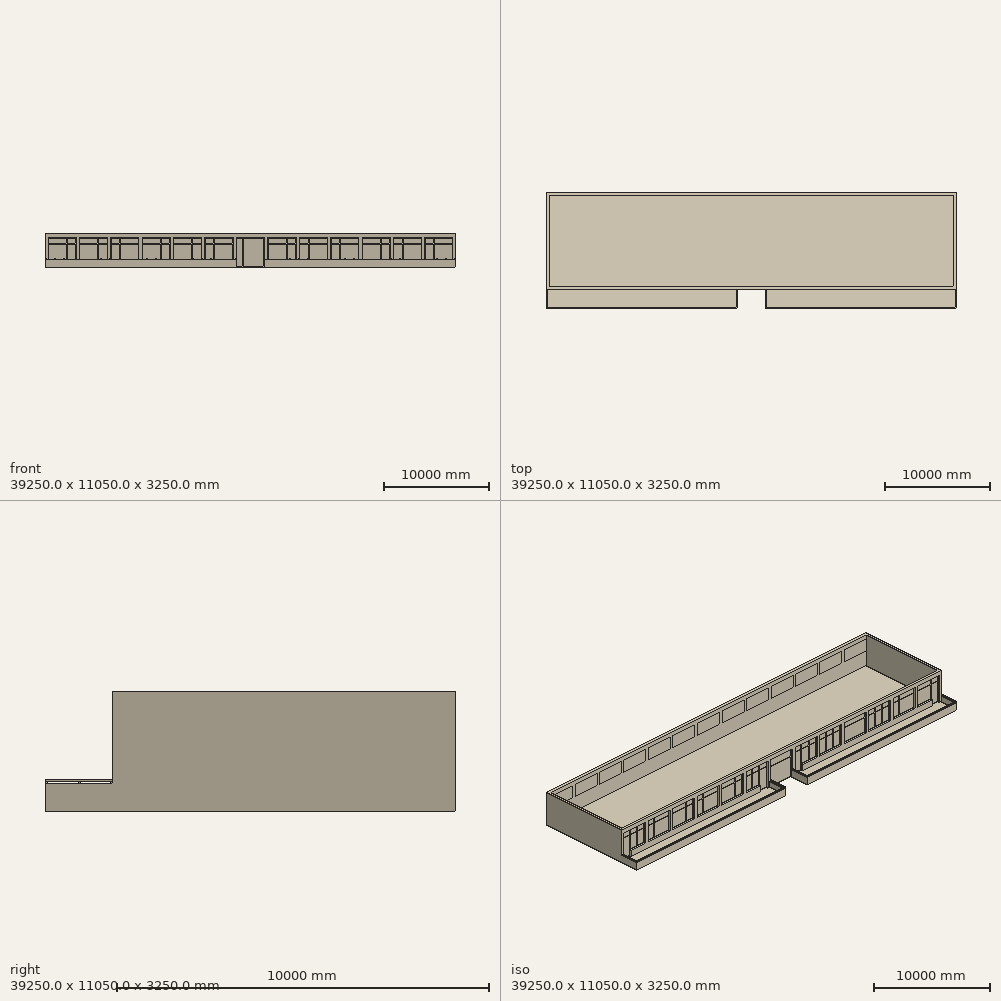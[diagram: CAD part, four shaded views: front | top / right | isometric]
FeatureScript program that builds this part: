
annotation { "Feature Type Name" : "Feature", "Feature Type Description" : "" }
export const myFeature = defineFeature(function(context is Context, id is Id, definition is map)
    precondition{}
    {
        {
            var Q0;
            Q0=qCreatedBy(makeId("Top.planeOp"),FACE);
            var sketch = newSketch(context, id + "F0", { "sketchPlane" : qUnion([Q0])});
            skLineSegment(sketch, "E0.bottom", {"start": v(0, 0) * mm, "end": v(39250, 0) * mm});
            skLineSegment(sketch, "E0.top", {"start": v(0, -9250) * mm, "end": v(39250, -9250) * mm});
            skLineSegment(sketch, "E0.left", {"start": v(0, 0) * mm, "end": v(0, -9250) * mm});
            skLineSegment(sketch, "E0.right", {"start": v(39250, 0) * mm, "end": v(39250, -9250) * mm});
            skSolve(sketch);
        }
        {
            var Q0;
            Q0=qSketchRegion(id+"F0",true);
            extrude(context, id + "F1", {"entities" : qUnion([Q0]), "depth" : 150 * mm, "offsetDistance" : 25 * mm});
        }
        {
            var Q0;
            Q0=makeQuery(id+"F1.opExtrude","CAP_FACE",FACE,{"disambiguationData":[OSD([sQuery(id+"F0.wireOp",EDGE,"E0.bottom"),sQuery(id+"F0.wireOp",EDGE,"E0.top"),sQuery(id+"F0.wireOp",EDGE,"E0.left"),sQuery(id+"F0.wireOp",EDGE,"E0.right")])],"isStart":false});
            var sketch = newSketch(context, id + "F2", { "sketchPlane" : qUnion([Q0])});
            skLineSegment(sketch, "E1.0.0", {"start": v(0, 0) * mm, "end": v(0, -9250) * mm});
            skLineSegment(sketch, "E1.0.1", {"start": v(0, -9250) * mm, "end": v(39250, -9250) * mm});
            skLineSegment(sketch, "E1.0.2", {"start": v(39250, -9250) * mm, "end": v(39250, 0) * mm});
            skLineSegment(sketch, "E1.0.3", {"start": v(39250, 0) * mm, "end": v(0, 0) * mm});
            skLineSegment(sketch, "E2.0", {"start": v(250, -250) * mm, "end": v(250, -9000) * mm});
            skLineSegment(sketch, "E2.1", {"start": v(39000, -250) * mm, "end": v(250, -250) * mm});
            skLineSegment(sketch, "E2.2", {"start": v(39000, -9000) * mm, "end": v(39000, -250) * mm});
            skLineSegment(sketch, "E2.3", {"start": v(250, -9000) * mm, "end": v(39000, -9000) * mm});
            skSolve(sketch);
        }
        {
            var Q0;
            Q0=qSketchRegion(id+"F2",true);
            extrude(context, id + "F3", {"entities" : qUnion([Q0]), "operationType" : NewBodyOperationType.ADD, "depth" : 3100 * mm, "offsetDistance" : 25 * mm});
        }
        {
            var Q0;
            Q0=makeQuery(id+"F3.boolean.opBoolean","MERGE",FACE,{"derivedFrom":[makeQuery(id+"F1.opExtrude","SWEPT_FACE",FACE,{"disambiguationData":[OSD([sQuery(id+"F0.wireOp",EDGE,"E0.top")])]}),makeQuery(id+"F3.opExtrude","SWEPT_FACE",FACE,{"disambiguationData":[OSD([sQuery(id+"F2.wireOp",EDGE,"E1.0.1")])]})]});
            var sketch = newSketch(context, id + "F4", { "sketchPlane" : qUnion([Q0])});
            skLineSegment(sketch, "E3", {"start": v(1150, 150) * mm, "end": v(250, 150) * mm});
            skLineSegment(sketch, "E4", {"start": v(250, 150) * mm, "end": v(250, 2850) * mm});
            skLineSegment(sketch, "E5", {"start": v(250, 2850) * mm, "end": v(2950, 2850) * mm});
            skLineSegment(sketch, "E6", {"start": v(2950, 2850) * mm, "end": v(2950, 750) * mm});
            skLineSegment(sketch, "E7", {"start": v(2950, 750) * mm, "end": v(1150, 750) * mm});
            skLineSegment(sketch, "E8", {"start": v(1150, 750) * mm, "end": v(1150, 150) * mm});
            skLineSegment(sketch, "E9.bottom", {"start": v(3250, 2850) * mm, "end": v(5950, 2850) * mm});
            skLineSegment(sketch, "E9.top", {"start": v(3250, 750) * mm, "end": v(5950, 750) * mm});
            skLineSegment(sketch, "E9.left", {"start": v(3250, 2850) * mm, "end": v(3250, 750) * mm});
            skLineSegment(sketch, "E9.right", {"start": v(5950, 2850) * mm, "end": v(5950, 750) * mm});
            skLineSegment(sketch, "E10.1.0.0", {"start": v(6250, 2850) * mm, "end": v(8950, 2850) * mm});
            skLineSegment(sketch, "E10.1.0.1", {"start": v(8950, 2850) * mm, "end": v(8950, 750) * mm});
            skLineSegment(sketch, "E10.1.0.2", {"start": v(6250, 2850) * mm, "end": v(6250, 750) * mm});
            skLineSegment(sketch, "E10.1.0.3", {"start": v(6250, 750) * mm, "end": v(8950, 750) * mm});
            skLineSegment(sketch, "E10.2.0.0", {"start": v(9250, 2850) * mm, "end": v(11950, 2850) * mm});
            skLineSegment(sketch, "E10.2.0.1", {"start": v(11950, 2850) * mm, "end": v(11950, 750) * mm});
            skLineSegment(sketch, "E10.2.0.2", {"start": v(9250, 2850) * mm, "end": v(9250, 750) * mm});
            skLineSegment(sketch, "E10.2.0.3", {"start": v(9250, 750) * mm, "end": v(11950, 750) * mm});
            skLineSegment(sketch, "E10.3.0.0", {"start": v(12250, 2850) * mm, "end": v(14950, 2850) * mm});
            skLineSegment(sketch, "E10.3.0.1", {"start": v(14950, 2850) * mm, "end": v(14950, 750) * mm});
            skLineSegment(sketch, "E10.3.0.2", {"start": v(12250, 2850) * mm, "end": v(12250, 750) * mm});
            skLineSegment(sketch, "E10.3.0.3", {"start": v(12250, 750) * mm, "end": v(14950, 750) * mm});
            skLineSegment(sketch, "E10.direction1", {"start": v(3250, 750) * mm, "end": v(6250, 750) * mm, "construction": true});
            skLineSegment(sketch, "E11", {"start": v(17050, 150) * mm, "end": v(17950, 150) * mm});
            skLineSegment(sketch, "E12", {"start": v(17950, 150) * mm, "end": v(17950, 2850) * mm});
            skLineSegment(sketch, "E13", {"start": v(17950, 2850) * mm, "end": v(15250, 2850) * mm});
            skLineSegment(sketch, "E14", {"start": v(15250, 2850) * mm, "end": v(15250, 750) * mm});
            skLineSegment(sketch, "E15", {"start": v(15250, 750) * mm, "end": v(17050, 750) * mm});
            skLineSegment(sketch, "E16", {"start": v(17050, 750) * mm, "end": v(17050, 150) * mm});
            skLineSegment(sketch, "E17.top", {"start": v(18250, 2850) * mm, "end": v(20950, 2850) * mm});
            skLineSegment(sketch, "E17.left", {"start": v(18250, 150) * mm, "end": v(18250, 2850) * mm});
            skLineSegment(sketch, "E17.right", {"start": v(20950, 150) * mm, "end": v(20950, 2850) * mm});
            skLineSegment(sketch, "E18", {"start": v(19625, 0) * mm, "end": v(19625, 3250) * mm, "construction": true});
            skLineSegment(sketch, "E19.MirrorCS", {"start": v(38100, 750) * mm, "end": v(38100, 150) * mm});
            skLineSegment(sketch, "E20.MirrorCS", {"start": v(22200, 750) * mm, "end": v(22200, 150) * mm});
            skLineSegment(sketch, "E21.MirrorCS", {"start": v(36000, 750) * mm, "end": v(33300, 750) * mm});
            skLineSegment(sketch, "E22.MirrorCS", {"start": v(21300, 2850) * mm, "end": v(24000, 2850) * mm});
            skLineSegment(sketch, "E23.MirrorCS", {"start": v(36000, 750) * mm, "end": v(33000, 750) * mm, "construction": true});
            skLineSegment(sketch, "E24.MirrorCS", {"start": v(27000, 2850) * mm, "end": v(24300, 2850) * mm});
            skLineSegment(sketch, "E25.MirrorCS", {"start": v(24000, 2850) * mm, "end": v(24000, 750) * mm});
            skLineSegment(sketch, "E26.MirrorCS", {"start": v(27000, 2850) * mm, "end": v(27000, 750) * mm});
            skLineSegment(sketch, "E27.MirrorCS", {"start": v(24000, 750) * mm, "end": v(22200, 750) * mm});
            skLineSegment(sketch, "E28.MirrorCS", {"start": v(33000, 750) * mm, "end": v(30300, 750) * mm});
            skLineSegment(sketch, "E29.MirrorCS", {"start": v(24300, 2850) * mm, "end": v(24300, 750) * mm});
            skLineSegment(sketch, "E30.MirrorCS", {"start": v(30000, 2850) * mm, "end": v(27300, 2850) * mm});
            skLineSegment(sketch, "E31.MirrorCS", {"start": v(38100, 150) * mm, "end": v(39000, 150) * mm});
            skLineSegment(sketch, "E32.MirrorCS", {"start": v(27300, 2850) * mm, "end": v(27300, 750) * mm});
            skLineSegment(sketch, "E33.MirrorCS", {"start": v(39000, 150) * mm, "end": v(39000, 2850) * mm});
            skLineSegment(sketch, "E34.MirrorCS", {"start": v(22200, 150) * mm, "end": v(21300, 150) * mm});
            skLineSegment(sketch, "E35.MirrorCS", {"start": v(39000, 2850) * mm, "end": v(36300, 2850) * mm});
            skLineSegment(sketch, "E36.MirrorCS", {"start": v(36300, 2850) * mm, "end": v(36300, 750) * mm});
            skLineSegment(sketch, "E37.MirrorCS", {"start": v(36300, 750) * mm, "end": v(38100, 750) * mm});
            skLineSegment(sketch, "E38.MirrorCS", {"start": v(36000, 2850) * mm, "end": v(33300, 2850) * mm});
            skLineSegment(sketch, "E39.MirrorCS", {"start": v(36000, 2850) * mm, "end": v(36000, 750) * mm});
            skLineSegment(sketch, "E40.MirrorCS", {"start": v(33300, 2850) * mm, "end": v(33300, 750) * mm});
            skLineSegment(sketch, "E41.MirrorCS", {"start": v(27000, 750) * mm, "end": v(24300, 750) * mm});
            skLineSegment(sketch, "E42.MirrorCS", {"start": v(30000, 2850) * mm, "end": v(30000, 750) * mm});
            skLineSegment(sketch, "E43.MirrorCS", {"start": v(30000, 750) * mm, "end": v(27300, 750) * mm});
            skLineSegment(sketch, "E44.MirrorCS", {"start": v(33000, 2850) * mm, "end": v(30300, 2850) * mm});
            skLineSegment(sketch, "E45.MirrorCS", {"start": v(21300, 150) * mm, "end": v(21300, 2850) * mm});
            skLineSegment(sketch, "E46.MirrorCS", {"start": v(30300, 2850) * mm, "end": v(30300, 750) * mm});
            skLineSegment(sketch, "E47.MirrorCS", {"start": v(33000, 2850) * mm, "end": v(33000, 750) * mm});
            skLineSegment(sketch, "E48", {"start": v(18250, 150) * mm, "end": v(18250, 0) * mm});
            skLineSegment(sketch, "E49", {"start": v(18250, 0) * mm, "end": v(20950, 0) * mm});
            skLineSegment(sketch, "E50", {"start": v(20950, 0) * mm, "end": v(20950, 150) * mm});
            skSolve(sketch);
        }
        {
            var Q0;
            Q0=qSketchRegion(id+"F4",true);
            extrude(context, id + "F5", {"entities" : qUnion([Q0]), "operationType" : NewBodyOperationType.REMOVE, "oppositeDirection" : true, "depth" : 300 * mm, "offsetDistance" : 25 * mm});
        }
        {
            var Q0;
            Q0=makeQuery(id+"F3.opExtrude","SWEPT_FACE",FACE,{"disambiguationData":[OSD([sQuery(id+"F2.wireOp",EDGE,"E2.3")])]});
            var sketch = newSketch(context, id + "F6", { "sketchPlane" : qUnion([Q0])});
            skLineSegment(sketch, "E51.0", {"start": v(-1150, 150) * mm, "end": v(-250, 150) * mm});
            skLineSegment(sketch, "E51.1", {"start": v(-250, 150) * mm, "end": v(-250, 2850) * mm});
            skLineSegment(sketch, "E51.2", {"start": v(-250, 2850) * mm, "end": v(-2950, 2850) * mm});
            skLineSegment(sketch, "E51.3", {"start": v(-2950, 2850) * mm, "end": v(-2950, 750) * mm});
            skLineSegment(sketch, "E51.4", {"start": v(-2950, 750) * mm, "end": v(-1150, 750) * mm});
            skLineSegment(sketch, "E51.5", {"start": v(-1150, 750) * mm, "end": v(-1150, 150) * mm});
            skLineSegment(sketch, "E51.6", {"start": v(-3250, 2850) * mm, "end": v(-5950, 2850) * mm});
            skLineSegment(sketch, "E51.7", {"start": v(-3250, 750) * mm, "end": v(-5950, 750) * mm});
            skLineSegment(sketch, "E51.8", {"start": v(-3250, 2850) * mm, "end": v(-3250, 750) * mm});
            skLineSegment(sketch, "E51.9", {"start": v(-5950, 2850) * mm, "end": v(-5950, 750) * mm});
            skLineSegment(sketch, "E51.10", {"start": v(-6250, 2850) * mm, "end": v(-8950, 2850) * mm});
            skLineSegment(sketch, "E51.11", {"start": v(-8950, 2850) * mm, "end": v(-8950, 750) * mm});
            skLineSegment(sketch, "E51.12", {"start": v(-6250, 2850) * mm, "end": v(-6250, 750) * mm});
            skLineSegment(sketch, "E51.13", {"start": v(-6250, 750) * mm, "end": v(-8950, 750) * mm});
            skLineSegment(sketch, "E51.14", {"start": v(-9250, 2850) * mm, "end": v(-11950, 2850) * mm});
            skLineSegment(sketch, "E51.15", {"start": v(-11950, 2850) * mm, "end": v(-11950, 750) * mm});
            skLineSegment(sketch, "E51.16", {"start": v(-9250, 2850) * mm, "end": v(-9250, 750) * mm});
            skLineSegment(sketch, "E51.17", {"start": v(-9250, 750) * mm, "end": v(-11950, 750) * mm});
            skLineSegment(sketch, "E51.18", {"start": v(-12250, 2850) * mm, "end": v(-14950, 2850) * mm});
            skLineSegment(sketch, "E51.19", {"start": v(-14950, 2850) * mm, "end": v(-14950, 750) * mm});
            skLineSegment(sketch, "E51.20", {"start": v(-12250, 2850) * mm, "end": v(-12250, 750) * mm});
            skLineSegment(sketch, "E51.21", {"start": v(-12250, 750) * mm, "end": v(-14950, 750) * mm});
            skLineSegment(sketch, "E51.22", {"start": v(-3250, 750) * mm, "end": v(-6250, 750) * mm});
            skLineSegment(sketch, "E51.23", {"start": v(-17050, 150) * mm, "end": v(-17950, 150) * mm});
            skLineSegment(sketch, "E51.24", {"start": v(-17950, 150) * mm, "end": v(-17950, 2850) * mm});
            skLineSegment(sketch, "E51.25", {"start": v(-17950, 2850) * mm, "end": v(-15250, 2850) * mm});
            skLineSegment(sketch, "E51.26", {"start": v(-15250, 2850) * mm, "end": v(-15250, 750) * mm});
            skLineSegment(sketch, "E51.27", {"start": v(-15250, 750) * mm, "end": v(-17050, 750) * mm});
            skLineSegment(sketch, "E51.28", {"start": v(-17050, 750) * mm, "end": v(-17050, 150) * mm});
            skLineSegment(sketch, "E51.30", {"start": v(-18250, 2850) * mm, "end": v(-20950, 2850) * mm});
            skLineSegment(sketch, "E51.31", {"start": v(-18250, 150) * mm, "end": v(-18250, 2850) * mm});
            skLineSegment(sketch, "E51.32", {"start": v(-20950, 150) * mm, "end": v(-20950, 2850) * mm});
            skLineSegment(sketch, "E51.33", {"start": v(-19625, 0) * mm, "end": v(-19625, 3250) * mm, "construction": true});
            skLineSegment(sketch, "E51.34", {"start": v(-38100, 750) * mm, "end": v(-38100, 150) * mm});
            skLineSegment(sketch, "E51.35", {"start": v(-22200, 750) * mm, "end": v(-22200, 150) * mm});
            skLineSegment(sketch, "E51.36", {"start": v(-36000, 750) * mm, "end": v(-33300, 750) * mm});
            skLineSegment(sketch, "E51.37", {"start": v(-21300, 2850) * mm, "end": v(-24000, 2850) * mm});
            skLineSegment(sketch, "E51.38", {"start": v(-36000, 750) * mm, "end": v(-33000, 750) * mm});
            skLineSegment(sketch, "E51.39", {"start": v(-27000, 2850) * mm, "end": v(-24300, 2850) * mm});
            skLineSegment(sketch, "E51.40", {"start": v(-24000, 2850) * mm, "end": v(-24000, 750) * mm});
            skLineSegment(sketch, "E51.41", {"start": v(-27000, 2850) * mm, "end": v(-27000, 750) * mm});
            skLineSegment(sketch, "E51.42", {"start": v(-24000, 750) * mm, "end": v(-22200, 750) * mm});
            skLineSegment(sketch, "E51.43", {"start": v(-33000, 750) * mm, "end": v(-30300, 750) * mm});
            skLineSegment(sketch, "E51.44", {"start": v(-24300, 2850) * mm, "end": v(-24300, 750) * mm});
            skLineSegment(sketch, "E51.45", {"start": v(-30000, 2850) * mm, "end": v(-27300, 2850) * mm});
            skLineSegment(sketch, "E51.46", {"start": v(-38100, 150) * mm, "end": v(-39000, 150) * mm});
            skLineSegment(sketch, "E51.47", {"start": v(-27300, 2850) * mm, "end": v(-27300, 750) * mm});
            skLineSegment(sketch, "E51.48", {"start": v(-39000, 150) * mm, "end": v(-39000, 2850) * mm});
            skLineSegment(sketch, "E51.49", {"start": v(-22200, 150) * mm, "end": v(-21300, 150) * mm});
            skLineSegment(sketch, "E51.50", {"start": v(-39000, 2850) * mm, "end": v(-36300, 2850) * mm});
            skLineSegment(sketch, "E51.51", {"start": v(-36300, 2850) * mm, "end": v(-36300, 750) * mm});
            skLineSegment(sketch, "E51.52", {"start": v(-36300, 750) * mm, "end": v(-38100, 750) * mm});
            skLineSegment(sketch, "E51.53", {"start": v(-36000, 2850) * mm, "end": v(-33300, 2850) * mm});
            skLineSegment(sketch, "E51.54", {"start": v(-36000, 2850) * mm, "end": v(-36000, 750) * mm});
            skLineSegment(sketch, "E51.55", {"start": v(-33300, 2850) * mm, "end": v(-33300, 750) * mm});
            skLineSegment(sketch, "E51.56", {"start": v(-27000, 750) * mm, "end": v(-24300, 750) * mm});
            skLineSegment(sketch, "E51.57", {"start": v(-30000, 2850) * mm, "end": v(-30000, 750) * mm});
            skLineSegment(sketch, "E51.58", {"start": v(-30000, 750) * mm, "end": v(-27300, 750) * mm});
            skLineSegment(sketch, "E51.59", {"start": v(-33000, 2850) * mm, "end": v(-30300, 2850) * mm});
            skLineSegment(sketch, "E51.60", {"start": v(-21300, 150) * mm, "end": v(-21300, 2850) * mm});
            skLineSegment(sketch, "E51.61", {"start": v(-30300, 2850) * mm, "end": v(-30300, 750) * mm});
            skLineSegment(sketch, "E51.62", {"start": v(-33000, 2850) * mm, "end": v(-33000, 750) * mm});
            skLineSegment(sketch, "E52.0", {"start": v(-20950, 0) * mm, "end": v(-20950, 150) * mm});
            skLineSegment(sketch, "E53.0", {"start": v(-18250, 0) * mm, "end": v(-20950, 0) * mm});
            skLineSegment(sketch, "E54.0", {"start": v(-18250, 0) * mm, "end": v(-18250, 150) * mm});
            skSolve(sketch);
        }
        {
            var Q0;
            Q0=qSketchRegion(id+"F6",true);
            extrude(context, id + "F7", {"entities" : qUnion([Q0]), "oppositeDirection" : true, "depth" : 50 * mm, "offsetDistance" : 25 * mm});
        }
        {
            var Q0;
            Q0=makeQuery(id+"F7.opExtrude","CAP_FACE",FACE,{"disambiguationData":[OSD([sQuery(id+"F6.wireOp",EDGE,"E51.0"),sQuery(id+"F6.wireOp",EDGE,"E51.1"),sQuery(id+"F6.wireOp",EDGE,"E51.2"),sQuery(id+"F6.wireOp",EDGE,"E51.3"),sQuery(id+"F6.wireOp",EDGE,"E51.4"),sQuery(id+"F6.wireOp",EDGE,"E51.5")])],"isStart":false});
            var sketch = newSketch(context, id + "F8", { "sketchPlane" : qUnion([Q0])});
            skPoint(sketch, "E55", {"position": v(250, 150) * mm});
            skLineSegment(sketch, "E56.bottom", {"start": v(300, 2200) * mm, "end": v(1112.5, 2200) * mm});
            skLineSegment(sketch, "E56.top", {"start": v(300, 200) * mm, "end": v(1112.5, 200) * mm});
            skLineSegment(sketch, "E56.left", {"start": v(300, 2200) * mm, "end": v(300, 200) * mm});
            skLineSegment(sketch, "E56.right", {"start": v(1112.5, 2200) * mm, "end": v(1112.5, 200) * mm});
            skLineSegment(sketch, "E57.bottom", {"start": v(300, 2250) * mm, "end": v(1112.5, 2250) * mm});
            skLineSegment(sketch, "E57.top", {"start": v(300, 2800) * mm, "end": v(1112.5, 2800) * mm});
            skLineSegment(sketch, "E57.left", {"start": v(300, 2250) * mm, "end": v(300, 2800) * mm});
            skLineSegment(sketch, "E57.right", {"start": v(1112.5, 2250) * mm, "end": v(1112.5, 2800) * mm});
            skLineSegment(sketch, "E58.0.0", {"start": v(250, 150) * mm, "end": v(1150, 150) * mm});
            skLineSegment(sketch, "E58.0.1", {"start": v(1150, 150) * mm, "end": v(1150, 750) * mm});
            skLineSegment(sketch, "E58.0.2", {"start": v(1150, 750) * mm, "end": v(2950, 750) * mm});
            skLineSegment(sketch, "E58.0.3", {"start": v(2950, 750) * mm, "end": v(2950, 2850) * mm});
            skLineSegment(sketch, "E58.0.4", {"start": v(2950, 2850) * mm, "end": v(250, 2850) * mm});
            skLineSegment(sketch, "E58.0.5", {"start": v(250, 2850) * mm, "end": v(250, 150) * mm});
            skLineSegment(sketch, "E59.bottom", {"start": v(1187.5, 2800) * mm, "end": v(2037.5, 2800) * mm});
            skLineSegment(sketch, "E59.top", {"start": v(1187.5, 2250) * mm, "end": v(2037.5, 2250) * mm});
            skLineSegment(sketch, "E59.left", {"start": v(1187.5, 2800) * mm, "end": v(1187.5, 2250) * mm});
            skLineSegment(sketch, "E59.right", {"start": v(2037.5, 2800) * mm, "end": v(2037.5, 2250) * mm});
            skLineSegment(sketch, "E60.bottom", {"start": v(2087.5, 2800) * mm, "end": v(2900, 2800) * mm});
            skLineSegment(sketch, "E60.top", {"start": v(2087.5, 2250) * mm, "end": v(2900, 2250) * mm});
            skLineSegment(sketch, "E60.left", {"start": v(2087.5, 2800) * mm, "end": v(2087.5, 2250) * mm});
            skLineSegment(sketch, "E60.right", {"start": v(2900, 2800) * mm, "end": v(2900, 2250) * mm});
            skLineSegment(sketch, "E61.bottom", {"start": v(1187.5, 2200) * mm, "end": v(2037.5, 2200) * mm});
            skLineSegment(sketch, "E61.top", {"start": v(1187.5, 800) * mm, "end": v(2037.5, 800) * mm});
            skLineSegment(sketch, "E61.left", {"start": v(1187.5, 2200) * mm, "end": v(1187.5, 800) * mm});
            skLineSegment(sketch, "E61.right", {"start": v(2037.5, 2200) * mm, "end": v(2037.5, 800) * mm});
            skLineSegment(sketch, "E62.bottom", {"start": v(2087.5, 2200) * mm, "end": v(2900, 2200) * mm});
            skLineSegment(sketch, "E62.top", {"start": v(2087.5, 800) * mm, "end": v(2900, 800) * mm});
            skLineSegment(sketch, "E62.left", {"start": v(2087.5, 2200) * mm, "end": v(2087.5, 800) * mm});
            skLineSegment(sketch, "E62.right", {"start": v(2900, 2200) * mm, "end": v(2900, 800) * mm});
            skLineSegment(sketch, "E63.bottom", {"start": v(3300, 2250) * mm, "end": v(4112.5, 2250) * mm});
            skLineSegment(sketch, "E63.top", {"start": v(3300, 2800) * mm, "end": v(4112.5, 2800) * mm});
            skLineSegment(sketch, "E63.left", {"start": v(3300, 2250) * mm, "end": v(3300, 2800) * mm});
            skLineSegment(sketch, "E63.right", {"start": v(4112.5, 2250) * mm, "end": v(4112.5, 2800) * mm});
            skLineSegment(sketch, "E64.bottom", {"start": v(4162.5, 2800) * mm, "end": v(5012.5, 2800) * mm});
            skLineSegment(sketch, "E64.top", {"start": v(4162.5, 2250) * mm, "end": v(5012.5, 2250) * mm});
            skLineSegment(sketch, "E64.left", {"start": v(4162.5, 2800) * mm, "end": v(4162.5, 2250) * mm});
            skLineSegment(sketch, "E64.right", {"start": v(5012.5, 2800) * mm, "end": v(5012.5, 2250) * mm});
            skLineSegment(sketch, "E65.bottom", {"start": v(5062.5, 2800) * mm, "end": v(5900, 2800) * mm});
            skLineSegment(sketch, "E65.top", {"start": v(5062.5, 2250) * mm, "end": v(5900, 2250) * mm});
            skLineSegment(sketch, "E65.left", {"start": v(5062.5, 2800) * mm, "end": v(5062.5, 2250) * mm});
            skLineSegment(sketch, "E65.right", {"start": v(5900, 2800) * mm, "end": v(5900, 2250) * mm});
            skLineSegment(sketch, "E66.bottom", {"start": v(4162.5, 2200) * mm, "end": v(5012.5, 2200) * mm});
            skLineSegment(sketch, "E66.top", {"start": v(4162.5, 800) * mm, "end": v(5012.5, 800) * mm});
            skLineSegment(sketch, "E66.left", {"start": v(4162.5, 2200) * mm, "end": v(4162.5, 800) * mm});
            skLineSegment(sketch, "E66.right", {"start": v(5012.5, 2200) * mm, "end": v(5012.5, 800) * mm});
            skLineSegment(sketch, "E67.bottom", {"start": v(5062.5, 2200) * mm, "end": v(5900, 2200) * mm});
            skLineSegment(sketch, "E67.top", {"start": v(5062.5, 800) * mm, "end": v(5900, 800) * mm});
            skLineSegment(sketch, "E67.left", {"start": v(5062.5, 2200) * mm, "end": v(5062.5, 800) * mm});
            skLineSegment(sketch, "E67.right", {"start": v(5900, 2200) * mm, "end": v(5900, 800) * mm});
            skLineSegment(sketch, "E68.0.0", {"start": v(3250, 750) * mm, "end": v(5950, 750) * mm});
            skLineSegment(sketch, "E68.0.1", {"start": v(5950, 750) * mm, "end": v(5950, 2850) * mm});
            skLineSegment(sketch, "E68.0.2", {"start": v(5950, 2850) * mm, "end": v(3250, 2850) * mm});
            skLineSegment(sketch, "E68.0.3", {"start": v(3250, 2850) * mm, "end": v(3250, 750) * mm});
            skLineSegment(sketch, "E69.bottom", {"start": v(4112.5, 2200) * mm, "end": v(3300, 2200) * mm});
            skLineSegment(sketch, "E69.top", {"start": v(4112.5, 800) * mm, "end": v(3300, 800) * mm});
            skLineSegment(sketch, "E69.left", {"start": v(4112.5, 2200) * mm, "end": v(4112.5, 800) * mm});
            skLineSegment(sketch, "E69.right", {"start": v(3300, 2200) * mm, "end": v(3300, 800) * mm});
            skLineSegment(sketch, "E70.1.0.0", {"start": v(8062.5, 2800) * mm, "end": v(8900, 2800) * mm});
            skLineSegment(sketch, "E70.1.0.1", {"start": v(7112.5, 2200) * mm, "end": v(6300, 2200) * mm});
            skLineSegment(sketch, "E70.1.0.2", {"start": v(6300, 2800) * mm, "end": v(7112.5, 2800) * mm});
            skLineSegment(sketch, "E70.1.0.3", {"start": v(8062.5, 800) * mm, "end": v(8900, 800) * mm});
            skLineSegment(sketch, "E70.1.0.4", {"start": v(6300, 2200) * mm, "end": v(6300, 800) * mm});
            skLineSegment(sketch, "E70.1.0.5", {"start": v(7162.5, 2800) * mm, "end": v(8012.5, 2800) * mm});
            skLineSegment(sketch, "E70.1.0.6", {"start": v(6250, 750) * mm, "end": v(8950, 750) * mm});
            skLineSegment(sketch, "E70.1.0.7", {"start": v(8900, 2800) * mm, "end": v(8900, 2250) * mm});
            skLineSegment(sketch, "E70.1.0.8", {"start": v(7162.5, 2200) * mm, "end": v(8012.5, 2200) * mm});
            skLineSegment(sketch, "E70.1.0.9", {"start": v(8950, 750) * mm, "end": v(8950, 2850) * mm});
            skLineSegment(sketch, "E70.1.0.10", {"start": v(7162.5, 2250) * mm, "end": v(8012.5, 2250) * mm});
            skLineSegment(sketch, "E70.1.0.11", {"start": v(8062.5, 2800) * mm, "end": v(8062.5, 2250) * mm});
            skLineSegment(sketch, "E70.1.0.12", {"start": v(7112.5, 2200) * mm, "end": v(7112.5, 800) * mm});
            skLineSegment(sketch, "E70.1.0.13", {"start": v(8062.5, 2200) * mm, "end": v(8062.5, 800) * mm});
            skLineSegment(sketch, "E70.1.0.14", {"start": v(6300, 2250) * mm, "end": v(6300, 2800) * mm});
            skLineSegment(sketch, "E70.1.0.15", {"start": v(7162.5, 800) * mm, "end": v(8012.5, 800) * mm});
            skLineSegment(sketch, "E70.1.0.16", {"start": v(8012.5, 2200) * mm, "end": v(8012.5, 800) * mm});
            skLineSegment(sketch, "E70.1.0.17", {"start": v(8950, 2850) * mm, "end": v(6250, 2850) * mm});
            skLineSegment(sketch, "E70.1.0.18", {"start": v(7162.5, 2800) * mm, "end": v(7162.5, 2250) * mm});
            skLineSegment(sketch, "E70.1.0.19", {"start": v(7112.5, 800) * mm, "end": v(6300, 800) * mm});
            skLineSegment(sketch, "E70.1.0.20", {"start": v(8062.5, 2250) * mm, "end": v(8900, 2250) * mm});
            skLineSegment(sketch, "E70.1.0.21", {"start": v(8900, 2200) * mm, "end": v(8900, 800) * mm});
            skLineSegment(sketch, "E70.1.0.22", {"start": v(7112.5, 2250) * mm, "end": v(7112.5, 2800) * mm});
            skLineSegment(sketch, "E70.1.0.23", {"start": v(7162.5, 2200) * mm, "end": v(7162.5, 800) * mm});
            skLineSegment(sketch, "E70.1.0.24", {"start": v(6250, 2850) * mm, "end": v(6250, 750) * mm});
            skLineSegment(sketch, "E70.1.0.25", {"start": v(8062.5, 2200) * mm, "end": v(8900, 2200) * mm});
            skLineSegment(sketch, "E70.1.0.26", {"start": v(8012.5, 2800) * mm, "end": v(8012.5, 2250) * mm});
            skLineSegment(sketch, "E70.1.0.27", {"start": v(6300, 2250) * mm, "end": v(7112.5, 2250) * mm});
            skLineSegment(sketch, "E70.2.0.0", {"start": v(11062.5, 2800) * mm, "end": v(11900, 2800) * mm});
            skLineSegment(sketch, "E70.2.0.1", {"start": v(10112.5, 2200) * mm, "end": v(9300, 2200) * mm});
            skLineSegment(sketch, "E70.2.0.2", {"start": v(9300, 2800) * mm, "end": v(10112.5, 2800) * mm});
            skLineSegment(sketch, "E70.2.0.3", {"start": v(11062.5, 800) * mm, "end": v(11900, 800) * mm});
            skLineSegment(sketch, "E70.2.0.4", {"start": v(9300, 2200) * mm, "end": v(9300, 800) * mm});
            skLineSegment(sketch, "E70.2.0.5", {"start": v(10162.5, 2800) * mm, "end": v(11012.5, 2800) * mm});
            skLineSegment(sketch, "E70.2.0.6", {"start": v(9250, 750) * mm, "end": v(11950, 750) * mm});
            skLineSegment(sketch, "E70.2.0.7", {"start": v(11900, 2800) * mm, "end": v(11900, 2250) * mm});
            skLineSegment(sketch, "E70.2.0.8", {"start": v(10162.5, 2200) * mm, "end": v(11012.5, 2200) * mm});
            skLineSegment(sketch, "E70.2.0.9", {"start": v(11950, 750) * mm, "end": v(11950, 2850) * mm});
            skLineSegment(sketch, "E70.2.0.10", {"start": v(10162.5, 2250) * mm, "end": v(11012.5, 2250) * mm});
            skLineSegment(sketch, "E70.2.0.11", {"start": v(11062.5, 2800) * mm, "end": v(11062.5, 2250) * mm});
            skLineSegment(sketch, "E70.2.0.12", {"start": v(10112.5, 2200) * mm, "end": v(10112.5, 800) * mm});
            skLineSegment(sketch, "E70.2.0.13", {"start": v(11062.5, 2200) * mm, "end": v(11062.5, 800) * mm});
            skLineSegment(sketch, "E70.2.0.14", {"start": v(9300, 2250) * mm, "end": v(9300, 2800) * mm});
            skLineSegment(sketch, "E70.2.0.15", {"start": v(10162.5, 800) * mm, "end": v(11012.5, 800) * mm});
            skLineSegment(sketch, "E70.2.0.16", {"start": v(11012.5, 2200) * mm, "end": v(11012.5, 800) * mm});
            skLineSegment(sketch, "E70.2.0.17", {"start": v(11950, 2850) * mm, "end": v(9250, 2850) * mm});
            skLineSegment(sketch, "E70.2.0.18", {"start": v(10162.5, 2800) * mm, "end": v(10162.5, 2250) * mm});
            skLineSegment(sketch, "E70.2.0.19", {"start": v(10112.5, 800) * mm, "end": v(9300, 800) * mm});
            skLineSegment(sketch, "E70.2.0.20", {"start": v(11062.5, 2250) * mm, "end": v(11900, 2250) * mm});
            skLineSegment(sketch, "E70.2.0.21", {"start": v(11900, 2200) * mm, "end": v(11900, 800) * mm});
            skLineSegment(sketch, "E70.2.0.22", {"start": v(10112.5, 2250) * mm, "end": v(10112.5, 2800) * mm});
            skLineSegment(sketch, "E70.2.0.23", {"start": v(10162.5, 2200) * mm, "end": v(10162.5, 800) * mm});
            skLineSegment(sketch, "E70.2.0.24", {"start": v(9250, 2850) * mm, "end": v(9250, 750) * mm});
            skLineSegment(sketch, "E70.2.0.25", {"start": v(11062.5, 2200) * mm, "end": v(11900, 2200) * mm});
            skLineSegment(sketch, "E70.2.0.26", {"start": v(11012.5, 2800) * mm, "end": v(11012.5, 2250) * mm});
            skLineSegment(sketch, "E70.2.0.27", {"start": v(9300, 2250) * mm, "end": v(10112.5, 2250) * mm});
            skLineSegment(sketch, "E70.3.0.0", {"start": v(14062.5, 2800) * mm, "end": v(14900, 2800) * mm});
            skLineSegment(sketch, "E70.3.0.1", {"start": v(13112.5, 2200) * mm, "end": v(12300, 2200) * mm});
            skLineSegment(sketch, "E70.3.0.2", {"start": v(12300, 2800) * mm, "end": v(13112.5, 2800) * mm});
            skLineSegment(sketch, "E70.3.0.3", {"start": v(14062.5, 800) * mm, "end": v(14900, 800) * mm});
            skLineSegment(sketch, "E70.3.0.4", {"start": v(12300, 2200) * mm, "end": v(12300, 800) * mm});
            skLineSegment(sketch, "E70.3.0.5", {"start": v(13162.5, 2800) * mm, "end": v(14012.5, 2800) * mm});
            skLineSegment(sketch, "E70.3.0.6", {"start": v(12250, 750) * mm, "end": v(14950, 750) * mm});
            skLineSegment(sketch, "E70.3.0.7", {"start": v(14900, 2800) * mm, "end": v(14900, 2250) * mm});
            skLineSegment(sketch, "E70.3.0.8", {"start": v(13162.5, 2200) * mm, "end": v(14012.5, 2200) * mm});
            skLineSegment(sketch, "E70.3.0.9", {"start": v(14950, 750) * mm, "end": v(14950, 2850) * mm});
            skLineSegment(sketch, "E70.3.0.10", {"start": v(13162.5, 2250) * mm, "end": v(14012.5, 2250) * mm});
            skLineSegment(sketch, "E70.3.0.11", {"start": v(14062.5, 2800) * mm, "end": v(14062.5, 2250) * mm});
            skLineSegment(sketch, "E70.3.0.12", {"start": v(13112.5, 2200) * mm, "end": v(13112.5, 800) * mm});
            skLineSegment(sketch, "E70.3.0.13", {"start": v(14062.5, 2200) * mm, "end": v(14062.5, 800) * mm});
            skLineSegment(sketch, "E70.3.0.14", {"start": v(12300, 2250) * mm, "end": v(12300, 2800) * mm});
            skLineSegment(sketch, "E70.3.0.15", {"start": v(13162.5, 800) * mm, "end": v(14012.5, 800) * mm});
            skLineSegment(sketch, "E70.3.0.16", {"start": v(14012.5, 2200) * mm, "end": v(14012.5, 800) * mm});
            skLineSegment(sketch, "E70.3.0.17", {"start": v(14950, 2850) * mm, "end": v(12250, 2850) * mm});
            skLineSegment(sketch, "E70.3.0.18", {"start": v(13162.5, 2800) * mm, "end": v(13162.5, 2250) * mm});
            skLineSegment(sketch, "E70.3.0.19", {"start": v(13112.5, 800) * mm, "end": v(12300, 800) * mm});
            skLineSegment(sketch, "E70.3.0.20", {"start": v(14062.5, 2250) * mm, "end": v(14900, 2250) * mm});
            skLineSegment(sketch, "E70.3.0.21", {"start": v(14900, 2200) * mm, "end": v(14900, 800) * mm});
            skLineSegment(sketch, "E70.3.0.22", {"start": v(13112.5, 2250) * mm, "end": v(13112.5, 2800) * mm});
            skLineSegment(sketch, "E70.3.0.23", {"start": v(13162.5, 2200) * mm, "end": v(13162.5, 800) * mm});
            skLineSegment(sketch, "E70.3.0.24", {"start": v(12250, 2850) * mm, "end": v(12250, 750) * mm});
            skLineSegment(sketch, "E70.3.0.25", {"start": v(14062.5, 2200) * mm, "end": v(14900, 2200) * mm});
            skLineSegment(sketch, "E70.3.0.26", {"start": v(14012.5, 2800) * mm, "end": v(14012.5, 2250) * mm});
            skLineSegment(sketch, "E70.3.0.27", {"start": v(12300, 2250) * mm, "end": v(13112.5, 2250) * mm});
            skLineSegment(sketch, "E70.direction1", {"start": v(3250, 750) * mm, "end": v(6250, 750) * mm, "construction": true});
            skLineSegment(sketch, "E71", {"start": v(1150, 150) * mm, "end": v(17050, 150) * mm, "construction": true});
            skLineSegment(sketch, "E72", {"start": v(9100, 150) * mm, "end": v(9100, 4213.1) * mm, "construction": true});
            skLineSegment(sketch, "E73.MirrorCS", {"start": v(17012.5, 2800) * mm, "end": v(16162.5, 2800) * mm});
            skLineSegment(sketch, "E74.MirrorCS", {"start": v(17900, 200) * mm, "end": v(17087.5, 200) * mm});
            skLineSegment(sketch, "E75.MirrorCS", {"start": v(17900, 2800) * mm, "end": v(17087.5, 2800) * mm});
            skLineSegment(sketch, "E76.MirrorCS", {"start": v(16112.5, 2800) * mm, "end": v(15300, 2800) * mm});
            skLineSegment(sketch, "E77.MirrorCS", {"start": v(17012.5, 2200) * mm, "end": v(17012.5, 800) * mm});
            skLineSegment(sketch, "E78.MirrorCS", {"start": v(17950, 2850) * mm, "end": v(17950, 150) * mm});
            skLineSegment(sketch, "E79.MirrorCS", {"start": v(17012.5, 2250) * mm, "end": v(16162.5, 2250) * mm});
            skLineSegment(sketch, "E80.MirrorCS", {"start": v(17900, 2200) * mm, "end": v(17087.5, 2200) * mm});
            skLineSegment(sketch, "E81.MirrorCS", {"start": v(17900, 2200) * mm, "end": v(17900, 200) * mm});
            skLineSegment(sketch, "E82.MirrorCS", {"start": v(17087.5, 2200) * mm, "end": v(17087.5, 200) * mm});
            skLineSegment(sketch, "E83.MirrorCS", {"start": v(17900, 2250) * mm, "end": v(17087.5, 2250) * mm});
            skLineSegment(sketch, "E84.MirrorCS", {"start": v(17900, 2250) * mm, "end": v(17900, 2800) * mm});
            skLineSegment(sketch, "E85.MirrorCS", {"start": v(17087.5, 2250) * mm, "end": v(17087.5, 2800) * mm});
            skLineSegment(sketch, "E86.MirrorCS", {"start": v(16162.5, 2200) * mm, "end": v(16162.5, 800) * mm});
            skLineSegment(sketch, "E87.MirrorCS", {"start": v(17950, 150) * mm, "end": v(17050, 150) * mm});
            skLineSegment(sketch, "E88.MirrorCS", {"start": v(17050, 150) * mm, "end": v(17050, 750) * mm});
            skLineSegment(sketch, "E89.MirrorCS", {"start": v(17050, 750) * mm, "end": v(15250, 750) * mm});
            skLineSegment(sketch, "E90.MirrorCS", {"start": v(15250, 750) * mm, "end": v(15250, 2850) * mm});
            skLineSegment(sketch, "E91.MirrorCS", {"start": v(15250, 2850) * mm, "end": v(17950, 2850) * mm});
            skLineSegment(sketch, "E92.MirrorCS", {"start": v(16112.5, 2200) * mm, "end": v(15300, 2200) * mm});
            skLineSegment(sketch, "E93.MirrorCS", {"start": v(16112.5, 800) * mm, "end": v(15300, 800) * mm});
            skLineSegment(sketch, "E94.MirrorCS", {"start": v(15300, 2200) * mm, "end": v(15300, 800) * mm});
            skLineSegment(sketch, "E95.MirrorCS", {"start": v(16112.5, 2200) * mm, "end": v(16112.5, 800) * mm});
            skLineSegment(sketch, "E96.MirrorCS", {"start": v(17012.5, 2800) * mm, "end": v(17012.5, 2250) * mm});
            skLineSegment(sketch, "E97.MirrorCS", {"start": v(16162.5, 2800) * mm, "end": v(16162.5, 2250) * mm});
            skLineSegment(sketch, "E98.MirrorCS", {"start": v(17012.5, 800) * mm, "end": v(16162.5, 800) * mm});
            skLineSegment(sketch, "E99.MirrorCS", {"start": v(16112.5, 2800) * mm, "end": v(16112.5, 2250) * mm});
            skLineSegment(sketch, "E100.MirrorCS", {"start": v(15300, 2800) * mm, "end": v(15300, 2250) * mm});
            skLineSegment(sketch, "E101.MirrorCS", {"start": v(16112.5, 2250) * mm, "end": v(15300, 2250) * mm});
            skLineSegment(sketch, "E102.MirrorCS", {"start": v(17012.5, 2200) * mm, "end": v(16162.5, 2200) * mm});
            skLineSegment(sketch, "E103", {"start": v(19825, -150) * mm, "end": v(19825, 5277.96) * mm, "construction": true});
            skLineSegment(sketch, "E104.MirrorCS", {"start": v(34187.5, 2800) * mm, "end": v(34187.5, 2250) * mm});
            skLineSegment(sketch, "E105.MirrorCS", {"start": v(29087.5, 2800) * mm, "end": v(29087.5, 2250) * mm});
            skLineSegment(sketch, "E106.MirrorCS", {"start": v(23087.5, 2800) * mm, "end": v(23087.5, 2250) * mm});
            skLineSegment(sketch, "E107.MirrorCS", {"start": v(25187.5, 2800) * mm, "end": v(25187.5, 2250) * mm});
            skLineSegment(sketch, "E108.MirrorCS", {"start": v(23137.5, 2800) * mm, "end": v(23137.5, 2250) * mm});
            skLineSegment(sketch, "E109.MirrorCS", {"start": v(25237.5, 2800) * mm, "end": v(25237.5, 2250) * mm});
            skLineSegment(sketch, "E110.MirrorCS", {"start": v(29137.5, 2250) * mm, "end": v(29137.5, 2800) * mm});
            skLineSegment(sketch, "E111.MirrorCS", {"start": v(35137.5, 2250) * mm, "end": v(35137.5, 2800) * mm});
            skLineSegment(sketch, "E112.MirrorCS", {"start": v(31237.5, 2800) * mm, "end": v(31237.5, 2250) * mm});
            skLineSegment(sketch, "E113.MirrorCS", {"start": v(35087.5, 2800) * mm, "end": v(35087.5, 2250) * mm});
            skLineSegment(sketch, "E114.MirrorCS", {"start": v(31187.5, 2800) * mm, "end": v(31187.5, 2250) * mm});
            skLineSegment(sketch, "E115.MirrorCS", {"start": v(34237.5, 2800) * mm, "end": v(34237.5, 2250) * mm});
            skLineSegment(sketch, "E116.MirrorCS", {"start": v(32950, 2250) * mm, "end": v(32950, 2800) * mm});
            skLineSegment(sketch, "E117.MirrorCS", {"start": v(26137.5, 2250) * mm, "end": v(26137.5, 2800) * mm});
            skLineSegment(sketch, "E118.MirrorCS", {"start": v(22237.5, 2800) * mm, "end": v(22237.5, 2250) * mm});
            skLineSegment(sketch, "E119.MirrorCS", {"start": v(38950, 2250) * mm, "end": v(38950, 2800) * mm});
            skLineSegment(sketch, "E120.MirrorCS", {"start": v(38137.5, 2250) * mm, "end": v(38137.5, 2800) * mm});
            skLineSegment(sketch, "E121.MirrorCS", {"start": v(38100, 150) * mm, "end": v(38100, 750) * mm});
            skLineSegment(sketch, "E122.MirrorCS", {"start": v(33350, 2800) * mm, "end": v(33350, 2250) * mm});
            skLineSegment(sketch, "E123.MirrorCS", {"start": v(24350, 2800) * mm, "end": v(24350, 2250) * mm});
            skLineSegment(sketch, "E124.MirrorCS", {"start": v(22162.5, 2250) * mm, "end": v(22162.5, 2800) * mm});
            skLineSegment(sketch, "E125.MirrorCS", {"start": v(35087.5, 800) * mm, "end": v(34237.5, 800) * mm});
            skLineSegment(sketch, "E126.MirrorCS", {"start": v(27350, 2800) * mm, "end": v(27350, 2250) * mm});
            skLineSegment(sketch, "E127.MirrorCS", {"start": v(32087.5, 2800) * mm, "end": v(32087.5, 2250) * mm});
            skLineSegment(sketch, "E128.MirrorCS", {"start": v(21350, 2250) * mm, "end": v(21350, 2800) * mm});
            skLineSegment(sketch, "E129.MirrorCS", {"start": v(23950, 2800) * mm, "end": v(23950, 2250) * mm});
            skLineSegment(sketch, "E130.MirrorCS", {"start": v(34187.5, 800) * mm, "end": v(33350, 800) * mm});
            skLineSegment(sketch, "E131.MirrorCS", {"start": v(35950, 2250) * mm, "end": v(35950, 2800) * mm});
            skLineSegment(sketch, "E132.MirrorCS", {"start": v(38062.5, 2800) * mm, "end": v(38062.5, 2250) * mm});
            skLineSegment(sketch, "E133.MirrorCS", {"start": v(28237.5, 2800) * mm, "end": v(28237.5, 2250) * mm});
            skLineSegment(sketch, "E134.MirrorCS", {"start": v(32137.5, 2250) * mm, "end": v(32137.5, 2800) * mm});
            skLineSegment(sketch, "E135.MirrorCS", {"start": v(22200, 150) * mm, "end": v(22200, 750) * mm});
            skLineSegment(sketch, "E136.MirrorCS", {"start": v(26950, 2250) * mm, "end": v(26950, 2800) * mm});
            skLineSegment(sketch, "E137.MirrorCS", {"start": v(37212.5, 2800) * mm, "end": v(37212.5, 2250) * mm});
            skLineSegment(sketch, "E138.MirrorCS", {"start": v(28187.5, 2800) * mm, "end": v(28187.5, 2250) * mm});
            skLineSegment(sketch, "E139.MirrorCS", {"start": v(30350, 2800) * mm, "end": v(30350, 2250) * mm});
            skLineSegment(sketch, "E140.MirrorCS", {"start": v(35137.5, 800) * mm, "end": v(35950, 800) * mm});
            skLineSegment(sketch, "E141.MirrorCS", {"start": v(36350, 2800) * mm, "end": v(36350, 2250) * mm});
            skLineSegment(sketch, "E142.MirrorCS", {"start": v(29950, 2250) * mm, "end": v(29950, 2800) * mm});
            skLineSegment(sketch, "E143.MirrorCS", {"start": v(37162.5, 2800) * mm, "end": v(37162.5, 2250) * mm});
            skLineSegment(sketch, "E144.MirrorCS", {"start": v(26087.5, 2800) * mm, "end": v(26087.5, 2250) * mm});
            skLineSegment(sketch, "E145.MirrorCS", {"start": v(35137.5, 2200) * mm, "end": v(35137.5, 800) * mm});
            skLineSegment(sketch, "E146.MirrorCS", {"start": v(21350, 2200) * mm, "end": v(22162.5, 2200) * mm});
            skLineSegment(sketch, "E147.MirrorCS", {"start": v(38062.5, 2800) * mm, "end": v(37212.5, 2800) * mm});
            skLineSegment(sketch, "E148.MirrorCS", {"start": v(38062.5, 2250) * mm, "end": v(37212.5, 2250) * mm});
            skLineSegment(sketch, "E149.MirrorCS", {"start": v(38950, 2200) * mm, "end": v(38137.5, 2200) * mm});
            skLineSegment(sketch, "E150.MirrorCS", {"start": v(28187.5, 800) * mm, "end": v(27350, 800) * mm});
            skLineSegment(sketch, "E151.MirrorCS", {"start": v(32087.5, 800) * mm, "end": v(31237.5, 800) * mm});
            skLineSegment(sketch, "E152.MirrorCS", {"start": v(21350, 2200) * mm, "end": v(21350, 200) * mm});
            skLineSegment(sketch, "E153.MirrorCS", {"start": v(29137.5, 800) * mm, "end": v(29950, 800) * mm});
            skLineSegment(sketch, "E154.MirrorCS", {"start": v(37162.5, 2200) * mm, "end": v(36350, 2200) * mm});
            skLineSegment(sketch, "E155.MirrorCS", {"start": v(31237.5, 2200) * mm, "end": v(31237.5, 800) * mm});
            skLineSegment(sketch, "E156.MirrorCS", {"start": v(35087.5, 2200) * mm, "end": v(34237.5, 2200) * mm});
            skLineSegment(sketch, "E157.MirrorCS", {"start": v(26087.5, 2200) * mm, "end": v(25237.5, 2200) * mm});
            skLineSegment(sketch, "E158.MirrorCS", {"start": v(22237.5, 800) * mm, "end": v(23087.5, 800) * mm});
            skLineSegment(sketch, "E159.MirrorCS", {"start": v(28187.5, 2250) * mm, "end": v(27350, 2250) * mm});
            skLineSegment(sketch, "E160.MirrorCS", {"start": v(23137.5, 2250) * mm, "end": v(23950, 2250) * mm});
            skLineSegment(sketch, "E161.MirrorCS", {"start": v(26950, 2250) * mm, "end": v(26137.5, 2250) * mm});
            skLineSegment(sketch, "E162.MirrorCS", {"start": v(37162.5, 800) * mm, "end": v(36350, 800) * mm});
            skLineSegment(sketch, "E163.MirrorCS", {"start": v(32137.5, 2200) * mm, "end": v(32950, 2200) * mm});
            skLineSegment(sketch, "E164.MirrorCS", {"start": v(25187.5, 2200) * mm, "end": v(24350, 2200) * mm});
            skLineSegment(sketch, "E165.MirrorCS", {"start": v(34237.5, 2200) * mm, "end": v(34237.5, 800) * mm});
            skLineSegment(sketch, "E166.MirrorCS", {"start": v(36350, 2200) * mm, "end": v(36350, 800) * mm});
            skLineSegment(sketch, "E167.MirrorCS", {"start": v(29087.5, 2200) * mm, "end": v(29087.5, 800) * mm});
            skLineSegment(sketch, "E168.MirrorCS", {"start": v(32137.5, 800) * mm, "end": v(32950, 800) * mm});
            skLineSegment(sketch, "E169.MirrorCS", {"start": v(31187.5, 800) * mm, "end": v(30350, 800) * mm});
            skLineSegment(sketch, "E170.MirrorCS", {"start": v(34187.5, 2200) * mm, "end": v(33350, 2200) * mm});
            skLineSegment(sketch, "E171.MirrorCS", {"start": v(35950, 2250) * mm, "end": v(35137.5, 2250) * mm});
            skLineSegment(sketch, "E172.MirrorCS", {"start": v(29087.5, 2200) * mm, "end": v(28237.5, 2200) * mm});
            skLineSegment(sketch, "E173.MirrorCS", {"start": v(31187.5, 2250) * mm, "end": v(30350, 2250) * mm});
            skLineSegment(sketch, "E174.MirrorCS", {"start": v(32950, 2200) * mm, "end": v(32950, 800) * mm});
            skLineSegment(sketch, "E175.MirrorCS", {"start": v(22237.5, 2200) * mm, "end": v(23087.5, 2200) * mm});
            skLineSegment(sketch, "E176.MirrorCS", {"start": v(23087.5, 2200) * mm, "end": v(23087.5, 800) * mm});
            skLineSegment(sketch, "E177.MirrorCS", {"start": v(30350, 2200) * mm, "end": v(30350, 800) * mm});
            skLineSegment(sketch, "E178.MirrorCS", {"start": v(25187.5, 2200) * mm, "end": v(25187.5, 800) * mm});
            skLineSegment(sketch, "E179.MirrorCS", {"start": v(29950, 2250) * mm, "end": v(29137.5, 2250) * mm});
            skLineSegment(sketch, "E180.MirrorCS", {"start": v(26087.5, 800) * mm, "end": v(25237.5, 800) * mm});
            skLineSegment(sketch, "E181.MirrorCS", {"start": v(36000, 750) * mm, "end": v(33300, 750) * mm});
            skLineSegment(sketch, "E182.MirrorCS", {"start": v(35087.5, 2800) * mm, "end": v(34237.5, 2800) * mm});
            skLineSegment(sketch, "E183.MirrorCS", {"start": v(32087.5, 2200) * mm, "end": v(31237.5, 2200) * mm});
            skLineSegment(sketch, "E184.MirrorCS", {"start": v(25187.5, 800) * mm, "end": v(24350, 800) * mm});
            skLineSegment(sketch, "E185.MirrorCS", {"start": v(29087.5, 800) * mm, "end": v(28237.5, 800) * mm});
            skLineSegment(sketch, "E186.MirrorCS", {"start": v(38062.5, 800) * mm, "end": v(37212.5, 800) * mm});
            skLineSegment(sketch, "E187.MirrorCS", {"start": v(26137.5, 800) * mm, "end": v(26950, 800) * mm});
            skLineSegment(sketch, "E188.MirrorCS", {"start": v(26950, 2200) * mm, "end": v(26950, 800) * mm});
            skLineSegment(sketch, "E189.MirrorCS", {"start": v(38062.5, 2200) * mm, "end": v(38062.5, 800) * mm});
            skLineSegment(sketch, "E190.MirrorCS", {"start": v(29950, 2800) * mm, "end": v(29137.5, 2800) * mm});
            skLineSegment(sketch, "E191.MirrorCS", {"start": v(39000, 2850) * mm, "end": v(39000, 150) * mm});
            skLineSegment(sketch, "E192.MirrorCS", {"start": v(27000, 750) * mm, "end": v(24300, 750) * mm});
            skLineSegment(sketch, "E193.MirrorCS", {"start": v(38950, 200) * mm, "end": v(38137.5, 200) * mm});
            skLineSegment(sketch, "E194.MirrorCS", {"start": v(38950, 2200) * mm, "end": v(38950, 200) * mm});
            skLineSegment(sketch, "E195.MirrorCS", {"start": v(38137.5, 2200) * mm, "end": v(38137.5, 200) * mm});
            skLineSegment(sketch, "E196.MirrorCS", {"start": v(38950, 2250) * mm, "end": v(38137.5, 2250) * mm});
            skLineSegment(sketch, "E197.MirrorCS", {"start": v(38950, 2800) * mm, "end": v(38137.5, 2800) * mm});
            skLineSegment(sketch, "E198.MirrorCS", {"start": v(37212.5, 2200) * mm, "end": v(37212.5, 800) * mm});
            skLineSegment(sketch, "E199.MirrorCS", {"start": v(39000, 150) * mm, "end": v(38100, 150) * mm});
            skLineSegment(sketch, "E200.MirrorCS", {"start": v(38100, 750) * mm, "end": v(36300, 750) * mm});
            skLineSegment(sketch, "E201.MirrorCS", {"start": v(36300, 750) * mm, "end": v(36300, 2850) * mm});
            skLineSegment(sketch, "E202.MirrorCS", {"start": v(36300, 2850) * mm, "end": v(39000, 2850) * mm});
            skLineSegment(sketch, "E203.MirrorCS", {"start": v(35950, 2200) * mm, "end": v(35950, 800) * mm});
            skLineSegment(sketch, "E204.MirrorCS", {"start": v(26087.5, 2200) * mm, "end": v(26087.5, 800) * mm});
            skLineSegment(sketch, "E205.MirrorCS", {"start": v(29950, 2200) * mm, "end": v(29950, 800) * mm});
            skLineSegment(sketch, "E206.MirrorCS", {"start": v(31187.5, 2800) * mm, "end": v(30350, 2800) * mm});
            skLineSegment(sketch, "E207.MirrorCS", {"start": v(22162.5, 2200) * mm, "end": v(22162.5, 200) * mm});
            skLineSegment(sketch, "E208.MirrorCS", {"start": v(27000, 2850) * mm, "end": v(27000, 750) * mm});
            skLineSegment(sketch, "E209.MirrorCS", {"start": v(29087.5, 2800) * mm, "end": v(28237.5, 2800) * mm});
            skLineSegment(sketch, "E210.MirrorCS", {"start": v(30300, 2850) * mm, "end": v(33000, 2850) * mm});
            skLineSegment(sketch, "E211.MirrorCS", {"start": v(21350, 2250) * mm, "end": v(22162.5, 2250) * mm});
            skLineSegment(sketch, "E212.MirrorCS", {"start": v(24300, 750) * mm, "end": v(24300, 2850) * mm});
            skLineSegment(sketch, "E213.MirrorCS", {"start": v(27350, 2200) * mm, "end": v(27350, 800) * mm});
            skLineSegment(sketch, "E214.MirrorCS", {"start": v(37162.5, 2200) * mm, "end": v(37162.5, 800) * mm});
            skLineSegment(sketch, "E215.MirrorCS", {"start": v(30000, 750) * mm, "end": v(27300, 750) * mm});
            skLineSegment(sketch, "E216.MirrorCS", {"start": v(32950, 2800) * mm, "end": v(32137.5, 2800) * mm});
            skLineSegment(sketch, "E217.MirrorCS", {"start": v(35087.5, 2200) * mm, "end": v(35087.5, 800) * mm});
            skLineSegment(sketch, "E218.MirrorCS", {"start": v(26087.5, 2250) * mm, "end": v(25237.5, 2250) * mm});
            skLineSegment(sketch, "E219.MirrorCS", {"start": v(30000, 2850) * mm, "end": v(30000, 750) * mm});
            skLineSegment(sketch, "E220.MirrorCS", {"start": v(36000, 750) * mm, "end": v(33000, 750) * mm, "construction": true});
            skLineSegment(sketch, "E221.MirrorCS", {"start": v(26137.5, 2200) * mm, "end": v(26137.5, 800) * mm});
            skLineSegment(sketch, "E222.MirrorCS", {"start": v(35950, 2800) * mm, "end": v(35137.5, 2800) * mm});
            skLineSegment(sketch, "E223.MirrorCS", {"start": v(28187.5, 2200) * mm, "end": v(27350, 2200) * mm});
            skLineSegment(sketch, "E224.MirrorCS", {"start": v(27300, 750) * mm, "end": v(27300, 2850) * mm});
            skLineSegment(sketch, "E225.MirrorCS", {"start": v(32087.5, 2800) * mm, "end": v(31237.5, 2800) * mm});
            skLineSegment(sketch, "E226.MirrorCS", {"start": v(21300, 150) * mm, "end": v(22200, 150) * mm});
            skLineSegment(sketch, "E227.MirrorCS", {"start": v(38100, 150) * mm, "end": v(22200, 150) * mm, "construction": true});
            skLineSegment(sketch, "E228.MirrorCS", {"start": v(34187.5, 2200) * mm, "end": v(34187.5, 800) * mm});
            skLineSegment(sketch, "E229.MirrorCS", {"start": v(29087.5, 2250) * mm, "end": v(28237.5, 2250) * mm});
            skLineSegment(sketch, "E230.MirrorCS", {"start": v(33000, 750) * mm, "end": v(30300, 750) * mm});
            skLineSegment(sketch, "E231.MirrorCS", {"start": v(30550, 150) * mm, "end": v(30550, 4213.1) * mm, "construction": true});
            skLineSegment(sketch, "E232.MirrorCS", {"start": v(33350, 2200) * mm, "end": v(33350, 800) * mm});
            skLineSegment(sketch, "E233.MirrorCS", {"start": v(32087.5, 2200) * mm, "end": v(32087.5, 800) * mm});
            skLineSegment(sketch, "E234.MirrorCS", {"start": v(22200, 750) * mm, "end": v(24000, 750) * mm});
            skLineSegment(sketch, "E235.MirrorCS", {"start": v(22237.5, 2800) * mm, "end": v(23087.5, 2800) * mm});
            skLineSegment(sketch, "E236.MirrorCS", {"start": v(37162.5, 2800) * mm, "end": v(36350, 2800) * mm});
            skLineSegment(sketch, "E237.MirrorCS", {"start": v(25187.5, 2800) * mm, "end": v(24350, 2800) * mm});
            skLineSegment(sketch, "E238.MirrorCS", {"start": v(29137.5, 2200) * mm, "end": v(29137.5, 800) * mm});
            skLineSegment(sketch, "E239.MirrorCS", {"start": v(33000, 2850) * mm, "end": v(33000, 750) * mm});
            skLineSegment(sketch, "E240.MirrorCS", {"start": v(24000, 750) * mm, "end": v(24000, 2850) * mm});
            skLineSegment(sketch, "E241.MirrorCS", {"start": v(21350, 200) * mm, "end": v(22162.5, 200) * mm});
            skLineSegment(sketch, "E242.MirrorCS", {"start": v(25237.5, 2200) * mm, "end": v(25237.5, 800) * mm});
            skLineSegment(sketch, "E243.MirrorCS", {"start": v(36000, 2850) * mm, "end": v(36000, 750) * mm});
            skLineSegment(sketch, "E244.MirrorCS", {"start": v(31187.5, 2200) * mm, "end": v(31187.5, 800) * mm});
            skLineSegment(sketch, "E245.MirrorCS", {"start": v(24350, 2200) * mm, "end": v(24350, 800) * mm});
            skLineSegment(sketch, "E246.MirrorCS", {"start": v(27300, 2850) * mm, "end": v(30000, 2850) * mm});
            skLineSegment(sketch, "E247.MirrorCS", {"start": v(32950, 2250) * mm, "end": v(32137.5, 2250) * mm});
            skLineSegment(sketch, "E248.MirrorCS", {"start": v(29137.5, 2200) * mm, "end": v(29950, 2200) * mm});
            skLineSegment(sketch, "E249.MirrorCS", {"start": v(32087.5, 2250) * mm, "end": v(31237.5, 2250) * mm});
            skLineSegment(sketch, "E250.MirrorCS", {"start": v(22237.5, 2250) * mm, "end": v(23087.5, 2250) * mm});
            skLineSegment(sketch, "E251.MirrorCS", {"start": v(26950, 2800) * mm, "end": v(26137.5, 2800) * mm});
            skLineSegment(sketch, "E252.MirrorCS", {"start": v(33300, 2850) * mm, "end": v(36000, 2850) * mm});
            skLineSegment(sketch, "E253.MirrorCS", {"start": v(34187.5, 2800) * mm, "end": v(33350, 2800) * mm});
            skLineSegment(sketch, "E254.MirrorCS", {"start": v(28187.5, 2200) * mm, "end": v(28187.5, 800) * mm});
            skLineSegment(sketch, "E255.MirrorCS", {"start": v(26137.5, 2200) * mm, "end": v(26950, 2200) * mm});
            skLineSegment(sketch, "E256.MirrorCS", {"start": v(31187.5, 2200) * mm, "end": v(30350, 2200) * mm});
            skLineSegment(sketch, "E257.MirrorCS", {"start": v(30300, 750) * mm, "end": v(30300, 2850) * mm});
            skLineSegment(sketch, "E258.MirrorCS", {"start": v(24000, 2850) * mm, "end": v(21300, 2850) * mm});
            skLineSegment(sketch, "E259.MirrorCS", {"start": v(35137.5, 2200) * mm, "end": v(35950, 2200) * mm});
            skLineSegment(sketch, "E260.MirrorCS", {"start": v(21350, 2800) * mm, "end": v(22162.5, 2800) * mm});
            skLineSegment(sketch, "E261.MirrorCS", {"start": v(24300, 2850) * mm, "end": v(27000, 2850) * mm});
            skLineSegment(sketch, "E262.MirrorCS", {"start": v(38062.5, 2200) * mm, "end": v(37212.5, 2200) * mm});
            skLineSegment(sketch, "E263.MirrorCS", {"start": v(35087.5, 2250) * mm, "end": v(34237.5, 2250) * mm});
            skLineSegment(sketch, "E264.MirrorCS", {"start": v(33300, 750) * mm, "end": v(33300, 2850) * mm});
            skLineSegment(sketch, "E265.MirrorCS", {"start": v(28237.5, 2200) * mm, "end": v(28237.5, 800) * mm});
            skLineSegment(sketch, "E266.MirrorCS", {"start": v(28187.5, 2800) * mm, "end": v(27350, 2800) * mm});
            skLineSegment(sketch, "E267.MirrorCS", {"start": v(32137.5, 2200) * mm, "end": v(32137.5, 800) * mm});
            skLineSegment(sketch, "E268.MirrorCS", {"start": v(21300, 2850) * mm, "end": v(21300, 150) * mm});
            skLineSegment(sketch, "E269.MirrorCS", {"start": v(34187.5, 2250) * mm, "end": v(33350, 2250) * mm});
            skLineSegment(sketch, "E270.MirrorCS", {"start": v(23137.5, 2200) * mm, "end": v(23950, 2200) * mm});
            skLineSegment(sketch, "E271.MirrorCS", {"start": v(23137.5, 2800) * mm, "end": v(23950, 2800) * mm});
            skLineSegment(sketch, "E272.MirrorCS", {"start": v(23137.5, 800) * mm, "end": v(23950, 800) * mm});
            skLineSegment(sketch, "E273.MirrorCS", {"start": v(22237.5, 2200) * mm, "end": v(22237.5, 800) * mm});
            skLineSegment(sketch, "E274.MirrorCS", {"start": v(23137.5, 2200) * mm, "end": v(23137.5, 800) * mm});
            skLineSegment(sketch, "E275.MirrorCS", {"start": v(25187.5, 2250) * mm, "end": v(24350, 2250) * mm});
            skLineSegment(sketch, "E276.MirrorCS", {"start": v(37162.5, 2250) * mm, "end": v(36350, 2250) * mm});
            skLineSegment(sketch, "E277.MirrorCS", {"start": v(26087.5, 2800) * mm, "end": v(25237.5, 2800) * mm});
            skLineSegment(sketch, "E278.MirrorCS", {"start": v(23950, 2200) * mm, "end": v(23950, 800) * mm});
            skLineSegment(sketch, "E279.bottom", {"start": v(18950, 2800) * mm, "end": v(20250, 2800) * mm});
            skLineSegment(sketch, "E279.top", {"start": v(18950, 50) * mm, "end": v(20250, 50) * mm});
            skLineSegment(sketch, "E279.left", {"start": v(18950, 2800) * mm, "end": v(18950, 2050) * mm});
            skLineSegment(sketch, "E279.right", {"start": v(20250, 2800) * mm, "end": v(20250, 2050) * mm});
            skLineSegment(sketch, "E280.bottom", {"start": v(18300, 2800) * mm, "end": v(18900, 2800) * mm});
            skLineSegment(sketch, "E280.top", {"start": v(18300, 50) * mm, "end": v(18900, 50) * mm});
            skLineSegment(sketch, "E280.left", {"start": v(18300, 2800) * mm, "end": v(18300, 2050) * mm});
            skLineSegment(sketch, "E280.right", {"start": v(18900, 2800) * mm, "end": v(18900, 2050) * mm});
            skLineSegment(sketch, "E281.bottom", {"start": v(20300, 2800) * mm, "end": v(20900, 2800) * mm});
            skLineSegment(sketch, "E281.top", {"start": v(20300, 50) * mm, "end": v(20900, 50) * mm});
            skLineSegment(sketch, "E281.left", {"start": v(20300, 2800) * mm, "end": v(20300, 2050) * mm});
            skLineSegment(sketch, "E281.right", {"start": v(20900, 2800) * mm, "end": v(20900, 2050) * mm});
            skLineSegment(sketch, "E282", {"start": v(18300, 2050) * mm, "end": v(18900, 2050) * mm});
            skLineSegment(sketch, "E283", {"start": v(18300, 2000) * mm, "end": v(18900, 2000) * mm});
            skLineSegment(sketch, "E284.trimOffspring", {"start": v(18300, 2000) * mm, "end": v(18300, 50) * mm});
            skLineSegment(sketch, "E285.trimOffspring", {"start": v(18900, 2000) * mm, "end": v(18900, 50) * mm});
            skLineSegment(sketch, "E286.trimOffspring", {"start": v(18950, 2050) * mm, "end": v(20250, 2050) * mm});
            skLineSegment(sketch, "E287.trimOffspring", {"start": v(18950, 2000) * mm, "end": v(18950, 50) * mm});
            skLineSegment(sketch, "E288.trimOffspring", {"start": v(18950, 2000) * mm, "end": v(20250, 2000) * mm});
            skLineSegment(sketch, "E289.trimOffspring", {"start": v(20300, 2050) * mm, "end": v(20900, 2050) * mm});
            skLineSegment(sketch, "E290.trimOffspring", {"start": v(20300, 2000) * mm, "end": v(20300, 50) * mm});
            skLineSegment(sketch, "E291.trimOffspring", {"start": v(20300, 2000) * mm, "end": v(20900, 2000) * mm});
            skLineSegment(sketch, "E292.trimOffspring", {"start": v(20250, 2000) * mm, "end": v(20250, 50) * mm});
            skLineSegment(sketch, "E293.trimOffspring", {"start": v(20900, 2000) * mm, "end": v(20900, 50) * mm});
            skLineSegment(sketch, "E294.0.0", {"start": v(18250, 0) * mm, "end": v(20950, 0) * mm});
            skLineSegment(sketch, "E294.0.1", {"start": v(20950, 0) * mm, "end": v(20950, 2850) * mm});
            skLineSegment(sketch, "E294.0.2", {"start": v(20950, 2850) * mm, "end": v(18250, 2850) * mm});
            skLineSegment(sketch, "E295", {"start": v(18250, 2850) * mm, "end": v(18250, 0) * mm});
            skLineSegment(sketch, "E296", {"start": v(20950, 2850) * mm, "end": v(20950, 0) * mm});
            skSolve(sketch);
        }
        {
            var Q0;
            Q0=qSketchRegion(id+"F8",true);
            extrude(context, id + "F9", {"entities" : qUnion([Q0]), "depth" : 25 * mm, "offsetDistance" : 25 * mm});
        }
        {
            var Q0;
            Q0=makeQuery(id+"F3.boolean.opBoolean","MERGE",FACE,{"derivedFrom":[makeQuery(id+"F1.opExtrude","SWEPT_FACE",FACE,{"disambiguationData":[OSD([sQuery(id+"F0.wireOp",EDGE,"E0.bottom")])]}),makeQuery(id+"F3.opExtrude","SWEPT_FACE",FACE,{"disambiguationData":[OSD([sQuery(id+"F2.wireOp",EDGE,"E1.0.3")])]})]});
            var sketch = newSketch(context, id + "F10", { "sketchPlane" : qUnion([Q0])});
            skLineSegment(sketch, "E297.bottom", {"start": v(-39000, 2850) * mm, "end": v(-36300, 2850) * mm});
            skLineSegment(sketch, "E297.top", {"start": v(-39000, 1650) * mm, "end": v(-36300, 1650) * mm});
            skLineSegment(sketch, "E297.left", {"start": v(-39000, 2850) * mm, "end": v(-39000, 1650) * mm});
            skLineSegment(sketch, "E297.right", {"start": v(-36300, 2850) * mm, "end": v(-36300, 1650) * mm});
            skLineSegment(sketch, "E298.1.0.0", {"start": v(-33300, 2850) * mm, "end": v(-33300, 1650) * mm});
            skLineSegment(sketch, "E298.1.0.1", {"start": v(-36000, 2850) * mm, "end": v(-36000, 1650) * mm});
            skLineSegment(sketch, "E298.1.0.2", {"start": v(-36000, 1650) * mm, "end": v(-33300, 1650) * mm});
            skLineSegment(sketch, "E298.1.0.3", {"start": v(-36000, 2850) * mm, "end": v(-33300, 2850) * mm});
            skLineSegment(sketch, "E298.2.0.0", {"start": v(-30300, 2850) * mm, "end": v(-30300, 1650) * mm});
            skLineSegment(sketch, "E298.2.0.1", {"start": v(-33000, 2850) * mm, "end": v(-33000, 1650) * mm});
            skLineSegment(sketch, "E298.2.0.2", {"start": v(-33000, 1650) * mm, "end": v(-30300, 1650) * mm});
            skLineSegment(sketch, "E298.2.0.3", {"start": v(-33000, 2850) * mm, "end": v(-30300, 2850) * mm});
            skLineSegment(sketch, "E298.3.0.0", {"start": v(-27300, 2850) * mm, "end": v(-27300, 1650) * mm});
            skLineSegment(sketch, "E298.3.0.1", {"start": v(-30000, 2850) * mm, "end": v(-30000, 1650) * mm});
            skLineSegment(sketch, "E298.3.0.2", {"start": v(-30000, 1650) * mm, "end": v(-27300, 1650) * mm});
            skLineSegment(sketch, "E298.3.0.3", {"start": v(-30000, 2850) * mm, "end": v(-27300, 2850) * mm});
            skLineSegment(sketch, "E298.4.0.0", {"start": v(-24300, 2850) * mm, "end": v(-24300, 1650) * mm});
            skLineSegment(sketch, "E298.4.0.1", {"start": v(-27000, 2850) * mm, "end": v(-27000, 1650) * mm});
            skLineSegment(sketch, "E298.4.0.2", {"start": v(-27000, 1650) * mm, "end": v(-24300, 1650) * mm});
            skLineSegment(sketch, "E298.4.0.3", {"start": v(-27000, 2850) * mm, "end": v(-24300, 2850) * mm});
            skLineSegment(sketch, "E298.5.0.0", {"start": v(-21300, 2850) * mm, "end": v(-21300, 1650) * mm});
            skLineSegment(sketch, "E298.5.0.1", {"start": v(-24000, 2850) * mm, "end": v(-24000, 1650) * mm});
            skLineSegment(sketch, "E298.5.0.2", {"start": v(-24000, 1650) * mm, "end": v(-21300, 1650) * mm});
            skLineSegment(sketch, "E298.5.0.3", {"start": v(-24000, 2850) * mm, "end": v(-21300, 2850) * mm});
            skLineSegment(sketch, "E298.direction1", {"start": v(-39000, 1650) * mm, "end": v(-36000, 1650) * mm, "construction": true});
            skLineSegment(sketch, "E299", {"start": v(-19625, 0) * mm, "end": v(-19625, 3250) * mm, "construction": true});
            skLineSegment(sketch, "E300.MirrorCS", {"start": v(-250, 1650) * mm, "end": v(-2950, 1650) * mm});
            skLineSegment(sketch, "E301.MirrorCS", {"start": v(-15250, 2850) * mm, "end": v(-17950, 2850) * mm});
            skLineSegment(sketch, "E302.MirrorCS", {"start": v(-12250, 2850) * mm, "end": v(-14950, 2850) * mm});
            skLineSegment(sketch, "E303.MirrorCS", {"start": v(-12250, 2850) * mm, "end": v(-12250, 1650) * mm});
            skLineSegment(sketch, "E304.MirrorCS", {"start": v(-15250, 2850) * mm, "end": v(-15250, 1650) * mm});
            skLineSegment(sketch, "E305.MirrorCS", {"start": v(-250, 1650) * mm, "end": v(-3250, 1650) * mm, "construction": true});
            skLineSegment(sketch, "E306.MirrorCS", {"start": v(-9250, 2850) * mm, "end": v(-9250, 1650) * mm});
            skLineSegment(sketch, "E307.MirrorCS", {"start": v(-12250, 1650) * mm, "end": v(-14950, 1650) * mm});
            skLineSegment(sketch, "E308.MirrorCS", {"start": v(-9250, 1650) * mm, "end": v(-11950, 1650) * mm});
            skLineSegment(sketch, "E309.MirrorCS", {"start": v(-9250, 2850) * mm, "end": v(-11950, 2850) * mm});
            skLineSegment(sketch, "E310.MirrorCS", {"start": v(-14950, 2850) * mm, "end": v(-14950, 1650) * mm});
            skLineSegment(sketch, "E311.MirrorCS", {"start": v(-250, 2850) * mm, "end": v(-2950, 2850) * mm});
            skLineSegment(sketch, "E312.MirrorCS", {"start": v(-250, 2850) * mm, "end": v(-250, 1650) * mm});
            skLineSegment(sketch, "E313.MirrorCS", {"start": v(-2950, 2850) * mm, "end": v(-2950, 1650) * mm});
            skLineSegment(sketch, "E314.MirrorCS", {"start": v(-5950, 2850) * mm, "end": v(-5950, 1650) * mm});
            skLineSegment(sketch, "E315.MirrorCS", {"start": v(-3250, 2850) * mm, "end": v(-3250, 1650) * mm});
            skLineSegment(sketch, "E316.MirrorCS", {"start": v(-3250, 1650) * mm, "end": v(-5950, 1650) * mm});
            skLineSegment(sketch, "E317.MirrorCS", {"start": v(-3250, 2850) * mm, "end": v(-5950, 2850) * mm});
            skLineSegment(sketch, "E318.MirrorCS", {"start": v(-15250, 1650) * mm, "end": v(-17950, 1650) * mm});
            skLineSegment(sketch, "E319.MirrorCS", {"start": v(-8950, 2850) * mm, "end": v(-8950, 1650) * mm});
            skLineSegment(sketch, "E320.MirrorCS", {"start": v(-6250, 2850) * mm, "end": v(-6250, 1650) * mm});
            skLineSegment(sketch, "E321.MirrorCS", {"start": v(-6250, 1650) * mm, "end": v(-8950, 1650) * mm});
            skLineSegment(sketch, "E322.MirrorCS", {"start": v(-6250, 2850) * mm, "end": v(-8950, 2850) * mm});
            skLineSegment(sketch, "E323.MirrorCS", {"start": v(-11950, 2850) * mm, "end": v(-11950, 1650) * mm});
            skLineSegment(sketch, "E324.MirrorCS", {"start": v(-17950, 2850) * mm, "end": v(-17950, 1650) * mm});
            skLineSegment(sketch, "E325.0.6.0", {"start": v(-18300, 2850) * mm, "end": v(-18300, 1650) * mm});
            skLineSegment(sketch, "E325.3.6.0", {"start": v(-21000, 2850) * mm, "end": v(-21000, 1650) * mm});
            skLineSegment(sketch, "E325.6.6.0", {"start": v(-21000, 1650) * mm, "end": v(-18300, 1650) * mm});
            skLineSegment(sketch, "E325.9.6.0", {"start": v(-21000, 2850) * mm, "end": v(-18300, 2850) * mm});
            skSolve(sketch);
        }
        {
            var Q0;
            Q0=qSketchRegion(id+"F10",true);
            extrude(context, id + "F11", {"entities" : qUnion([Q0]), "operationType" : NewBodyOperationType.REMOVE, "oppositeDirection" : true, "depth" : 300 * mm, "offsetDistance" : 25 * mm});
        }
        {
            var Q0;
            Q0=makeQuery(id+"F3.opExtrude","SWEPT_FACE",FACE,{"disambiguationData":[OSD([sQuery(id+"F2.wireOp",EDGE,"E2.1")])]});
            var sketch = newSketch(context, id + "F12", { "sketchPlane" : qUnion([Q0])});
            skLineSegment(sketch, "E326.0", {"start": v(39000, 2850) * mm, "end": v(36300, 2850) * mm});
            skLineSegment(sketch, "E326.1", {"start": v(39000, 1650) * mm, "end": v(36300, 1650) * mm});
            skLineSegment(sketch, "E326.2", {"start": v(39000, 2850) * mm, "end": v(39000, 1650) * mm});
            skLineSegment(sketch, "E326.3", {"start": v(36300, 2850) * mm, "end": v(36300, 1650) * mm});
            skLineSegment(sketch, "E326.4", {"start": v(33300, 2850) * mm, "end": v(33300, 1650) * mm});
            skLineSegment(sketch, "E326.5", {"start": v(36000, 2850) * mm, "end": v(36000, 1650) * mm});
            skLineSegment(sketch, "E326.6", {"start": v(36000, 1650) * mm, "end": v(33300, 1650) * mm});
            skLineSegment(sketch, "E326.7", {"start": v(36000, 2850) * mm, "end": v(33300, 2850) * mm});
            skLineSegment(sketch, "E326.8", {"start": v(30300, 2850) * mm, "end": v(30300, 1650) * mm});
            skLineSegment(sketch, "E326.9", {"start": v(33000, 2850) * mm, "end": v(33000, 1650) * mm});
            skLineSegment(sketch, "E326.10", {"start": v(33000, 1650) * mm, "end": v(30300, 1650) * mm});
            skLineSegment(sketch, "E326.11", {"start": v(33000, 2850) * mm, "end": v(30300, 2850) * mm});
            skLineSegment(sketch, "E326.12", {"start": v(27300, 2850) * mm, "end": v(27300, 1650) * mm});
            skLineSegment(sketch, "E326.13", {"start": v(30000, 2850) * mm, "end": v(30000, 1650) * mm});
            skLineSegment(sketch, "E326.14", {"start": v(30000, 1650) * mm, "end": v(27300, 1650) * mm});
            skLineSegment(sketch, "E326.15", {"start": v(30000, 2850) * mm, "end": v(27300, 2850) * mm});
            skLineSegment(sketch, "E326.16", {"start": v(24300, 2850) * mm, "end": v(24300, 1650) * mm});
            skLineSegment(sketch, "E326.17", {"start": v(27000, 2850) * mm, "end": v(27000, 1650) * mm});
            skLineSegment(sketch, "E326.18", {"start": v(27000, 1650) * mm, "end": v(24300, 1650) * mm});
            skLineSegment(sketch, "E326.19", {"start": v(27000, 2850) * mm, "end": v(24300, 2850) * mm});
            skLineSegment(sketch, "E326.20", {"start": v(21300, 2850) * mm, "end": v(21300, 1650) * mm});
            skLineSegment(sketch, "E326.21", {"start": v(24000, 2850) * mm, "end": v(24000, 1650) * mm});
            skLineSegment(sketch, "E326.22", {"start": v(24000, 1650) * mm, "end": v(21300, 1650) * mm});
            skLineSegment(sketch, "E326.23", {"start": v(24000, 2850) * mm, "end": v(21300, 2850) * mm});
            skLineSegment(sketch, "E326.24", {"start": v(39000, 1650) * mm, "end": v(36000, 1650) * mm});
            skLineSegment(sketch, "E326.25", {"start": v(19625, 0) * mm, "end": v(19625, 3250) * mm, "construction": true});
            skLineSegment(sketch, "E326.26", {"start": v(250, 1650) * mm, "end": v(2950, 1650) * mm});
            skLineSegment(sketch, "E326.27", {"start": v(15250, 2850) * mm, "end": v(17950, 2850) * mm});
            skLineSegment(sketch, "E326.28", {"start": v(12250, 2850) * mm, "end": v(14950, 2850) * mm});
            skLineSegment(sketch, "E326.29", {"start": v(12250, 2850) * mm, "end": v(12250, 1650) * mm});
            skLineSegment(sketch, "E326.30", {"start": v(15250, 2850) * mm, "end": v(15250, 1650) * mm});
            skLineSegment(sketch, "E326.31", {"start": v(250, 1650) * mm, "end": v(3250, 1650) * mm});
            skLineSegment(sketch, "E326.32", {"start": v(9250, 2850) * mm, "end": v(9250, 1650) * mm});
            skLineSegment(sketch, "E326.33", {"start": v(12250, 1650) * mm, "end": v(14950, 1650) * mm});
            skLineSegment(sketch, "E326.34", {"start": v(9250, 1650) * mm, "end": v(11950, 1650) * mm});
            skLineSegment(sketch, "E326.35", {"start": v(9250, 2850) * mm, "end": v(11950, 2850) * mm});
            skLineSegment(sketch, "E326.36", {"start": v(14950, 2850) * mm, "end": v(14950, 1650) * mm});
            skLineSegment(sketch, "E326.37", {"start": v(250, 2850) * mm, "end": v(2950, 2850) * mm});
            skLineSegment(sketch, "E326.38", {"start": v(250, 2850) * mm, "end": v(250, 1650) * mm});
            skLineSegment(sketch, "E326.39", {"start": v(2950, 2850) * mm, "end": v(2950, 1650) * mm});
            skLineSegment(sketch, "E326.40", {"start": v(5950, 2850) * mm, "end": v(5950, 1650) * mm});
            skLineSegment(sketch, "E326.41", {"start": v(3250, 2850) * mm, "end": v(3250, 1650) * mm});
            skLineSegment(sketch, "E326.42", {"start": v(3250, 1650) * mm, "end": v(5950, 1650) * mm});
            skLineSegment(sketch, "E326.43", {"start": v(3250, 2850) * mm, "end": v(5950, 2850) * mm});
            skLineSegment(sketch, "E326.44", {"start": v(15250, 1650) * mm, "end": v(17950, 1650) * mm});
            skLineSegment(sketch, "E326.45", {"start": v(8950, 2850) * mm, "end": v(8950, 1650) * mm});
            skLineSegment(sketch, "E326.46", {"start": v(6250, 2850) * mm, "end": v(6250, 1650) * mm});
            skLineSegment(sketch, "E326.47", {"start": v(6250, 1650) * mm, "end": v(8950, 1650) * mm});
            skLineSegment(sketch, "E326.48", {"start": v(6250, 2850) * mm, "end": v(8950, 2850) * mm});
            skLineSegment(sketch, "E326.49", {"start": v(11950, 2850) * mm, "end": v(11950, 1650) * mm});
            skLineSegment(sketch, "E326.50", {"start": v(17950, 2850) * mm, "end": v(17950, 1650) * mm});
            skLineSegment(sketch, "E327.0", {"start": v(21000, 2850) * mm, "end": v(18300, 2850) * mm});
            skLineSegment(sketch, "E328.0", {"start": v(21000, 1650) * mm, "end": v(21000, 2850) * mm});
            skLineSegment(sketch, "E329.0", {"start": v(21000, 1650) * mm, "end": v(18300, 1650) * mm});
            skLineSegment(sketch, "E330.0", {"start": v(18300, 2850) * mm, "end": v(18300, 1650) * mm});
            skSolve(sketch);
        }
        {
            var Q0;
            Q0=qSketchRegion(id+"F12",true);
            extrude(context, id + "F13", {"entities" : qUnion([Q0]), "oppositeDirection" : true, "depth" : 50 * mm, "offsetDistance" : 25 * mm});
        }
        {
            var Q0;
            Q0=makeQuery(id+"F13.opExtrude","CAP_FACE",FACE,{"disambiguationData":[OSD([sQuery(id+"F12.wireOp",EDGE,"E326.0"),sQuery(id+"F12.wireOp",EDGE,"E326.2"),sQuery(id+"F12.wireOp",EDGE,"E326.3"),sQuery(id+"F12.wireOp",EDGE,"E326.24")])],"isStart":false});
            var sketch = newSketch(context, id + "F14", { "sketchPlane" : qUnion([Q0])});
            skLineSegment(sketch, "E331.bottom", {"start": v(-38950, 2800) * mm, "end": v(-38350, 2800) * mm});
            skLineSegment(sketch, "E331.top", {"start": v(-38950, 1700) * mm, "end": v(-38350, 1700) * mm});
            skLineSegment(sketch, "E331.left", {"start": v(-38950, 2800) * mm, "end": v(-38950, 1700) * mm});
            skLineSegment(sketch, "E331.right", {"start": v(-38350, 2800) * mm, "end": v(-38350, 1700) * mm});
            skLineSegment(sketch, "E332", {"start": v(-37650, 1650) * mm, "end": v(-37650, 2850) * mm, "construction": true});
            skLineSegment(sketch, "E333.MirrorCS", {"start": v(-36950, 2800) * mm, "end": v(-36950, 1700) * mm});
            skLineSegment(sketch, "E334.MirrorCS", {"start": v(-36350, 2800) * mm, "end": v(-36350, 1700) * mm});
            skLineSegment(sketch, "E335.MirrorCS", {"start": v(-36350, 1700) * mm, "end": v(-36950, 1700) * mm});
            skLineSegment(sketch, "E336.MirrorCS", {"start": v(-36350, 2800) * mm, "end": v(-36950, 2800) * mm});
            skLineSegment(sketch, "E337.0.0", {"start": v(-39000, 2850) * mm, "end": v(-39000, 1650) * mm});
            skLineSegment(sketch, "E337.0.1", {"start": v(-39000, 1650) * mm, "end": v(-36300, 1650) * mm});
            skLineSegment(sketch, "E337.0.2", {"start": v(-36300, 1650) * mm, "end": v(-36300, 2850) * mm});
            skLineSegment(sketch, "E337.0.3", {"start": v(-36300, 2850) * mm, "end": v(-39000, 2850) * mm});
            skLineSegment(sketch, "E338.bottom", {"start": v(-38275, 2800) * mm, "end": v(-37025, 2800) * mm});
            skLineSegment(sketch, "E338.top", {"start": v(-38275, 1700) * mm, "end": v(-37025, 1700) * mm});
            skLineSegment(sketch, "E338.left", {"start": v(-38275, 2800) * mm, "end": v(-38275, 1700) * mm});
            skLineSegment(sketch, "E338.right", {"start": v(-37025, 2800) * mm, "end": v(-37025, 1700) * mm});
            skLineSegment(sketch, "E339.1.0.0", {"start": v(-34650, 1650) * mm, "end": v(-34650, 2850) * mm, "construction": true});
            skLineSegment(sketch, "E339.1.0.1", {"start": v(-33350, 2800) * mm, "end": v(-33950, 2800) * mm});
            skLineSegment(sketch, "E339.1.0.2", {"start": v(-33350, 1700) * mm, "end": v(-33950, 1700) * mm});
            skLineSegment(sketch, "E339.1.0.3", {"start": v(-33350, 2800) * mm, "end": v(-33350, 1700) * mm});
            skLineSegment(sketch, "E339.1.0.4", {"start": v(-33950, 2800) * mm, "end": v(-33950, 1700) * mm});
            skLineSegment(sketch, "E339.1.0.5", {"start": v(-36000, 2850) * mm, "end": v(-36000, 1650) * mm});
            skLineSegment(sketch, "E339.1.0.6", {"start": v(-36000, 1650) * mm, "end": v(-33300, 1650) * mm});
            skLineSegment(sketch, "E339.1.0.7", {"start": v(-34025, 2800) * mm, "end": v(-34025, 1700) * mm});
            skLineSegment(sketch, "E339.1.0.8", {"start": v(-33300, 1650) * mm, "end": v(-33300, 2850) * mm});
            skLineSegment(sketch, "E339.1.0.9", {"start": v(-33300, 2850) * mm, "end": v(-36000, 2850) * mm});
            skLineSegment(sketch, "E339.1.0.10", {"start": v(-35350, 2800) * mm, "end": v(-35350, 1700) * mm});
            skLineSegment(sketch, "E339.1.0.11", {"start": v(-35950, 2800) * mm, "end": v(-35950, 1700) * mm});
            skLineSegment(sketch, "E339.1.0.12", {"start": v(-35950, 1700) * mm, "end": v(-35350, 1700) * mm});
            skLineSegment(sketch, "E339.1.0.13", {"start": v(-35275, 1700) * mm, "end": v(-34025, 1700) * mm});
            skLineSegment(sketch, "E339.1.0.14", {"start": v(-35950, 2800) * mm, "end": v(-35350, 2800) * mm});
            skLineSegment(sketch, "E339.1.0.15", {"start": v(-35275, 2800) * mm, "end": v(-34025, 2800) * mm});
            skLineSegment(sketch, "E339.1.0.16", {"start": v(-35275, 2800) * mm, "end": v(-35275, 1700) * mm});
            skLineSegment(sketch, "E339.2.0.0", {"start": v(-31650, 1650) * mm, "end": v(-31650, 2850) * mm, "construction": true});
            skLineSegment(sketch, "E339.2.0.1", {"start": v(-30350, 2800) * mm, "end": v(-30950, 2800) * mm});
            skLineSegment(sketch, "E339.2.0.2", {"start": v(-30350, 1700) * mm, "end": v(-30950, 1700) * mm});
            skLineSegment(sketch, "E339.2.0.3", {"start": v(-30350, 2800) * mm, "end": v(-30350, 1700) * mm});
            skLineSegment(sketch, "E339.2.0.4", {"start": v(-30950, 2800) * mm, "end": v(-30950, 1700) * mm});
            skLineSegment(sketch, "E339.2.0.5", {"start": v(-33000, 2850) * mm, "end": v(-33000, 1650) * mm});
            skLineSegment(sketch, "E339.2.0.6", {"start": v(-33000, 1650) * mm, "end": v(-30300, 1650) * mm});
            skLineSegment(sketch, "E339.2.0.7", {"start": v(-31025, 2800) * mm, "end": v(-31025, 1700) * mm});
            skLineSegment(sketch, "E339.2.0.8", {"start": v(-30300, 1650) * mm, "end": v(-30300, 2850) * mm});
            skLineSegment(sketch, "E339.2.0.9", {"start": v(-30300, 2850) * mm, "end": v(-33000, 2850) * mm});
            skLineSegment(sketch, "E339.2.0.10", {"start": v(-32350, 2800) * mm, "end": v(-32350, 1700) * mm});
            skLineSegment(sketch, "E339.2.0.11", {"start": v(-32950, 2800) * mm, "end": v(-32950, 1700) * mm});
            skLineSegment(sketch, "E339.2.0.12", {"start": v(-32950, 1700) * mm, "end": v(-32350, 1700) * mm});
            skLineSegment(sketch, "E339.2.0.13", {"start": v(-32275, 1700) * mm, "end": v(-31025, 1700) * mm});
            skLineSegment(sketch, "E339.2.0.14", {"start": v(-32950, 2800) * mm, "end": v(-32350, 2800) * mm});
            skLineSegment(sketch, "E339.2.0.15", {"start": v(-32275, 2800) * mm, "end": v(-31025, 2800) * mm});
            skLineSegment(sketch, "E339.2.0.16", {"start": v(-32275, 2800) * mm, "end": v(-32275, 1700) * mm});
            skLineSegment(sketch, "E339.3.0.0", {"start": v(-28650, 1650) * mm, "end": v(-28650, 2850) * mm, "construction": true});
            skLineSegment(sketch, "E339.3.0.1", {"start": v(-27350, 2800) * mm, "end": v(-27950, 2800) * mm});
            skLineSegment(sketch, "E339.3.0.2", {"start": v(-27350, 1700) * mm, "end": v(-27950, 1700) * mm});
            skLineSegment(sketch, "E339.3.0.3", {"start": v(-27350, 2800) * mm, "end": v(-27350, 1700) * mm});
            skLineSegment(sketch, "E339.3.0.4", {"start": v(-27950, 2800) * mm, "end": v(-27950, 1700) * mm});
            skLineSegment(sketch, "E339.3.0.5", {"start": v(-30000, 2850) * mm, "end": v(-30000, 1650) * mm});
            skLineSegment(sketch, "E339.3.0.6", {"start": v(-30000, 1650) * mm, "end": v(-27300, 1650) * mm});
            skLineSegment(sketch, "E339.3.0.7", {"start": v(-28025, 2800) * mm, "end": v(-28025, 1700) * mm});
            skLineSegment(sketch, "E339.3.0.8", {"start": v(-27300, 1650) * mm, "end": v(-27300, 2850) * mm});
            skLineSegment(sketch, "E339.3.0.9", {"start": v(-27300, 2850) * mm, "end": v(-30000, 2850) * mm});
            skLineSegment(sketch, "E339.3.0.10", {"start": v(-29350, 2800) * mm, "end": v(-29350, 1700) * mm});
            skLineSegment(sketch, "E339.3.0.11", {"start": v(-29950, 2800) * mm, "end": v(-29950, 1700) * mm});
            skLineSegment(sketch, "E339.3.0.12", {"start": v(-29950, 1700) * mm, "end": v(-29350, 1700) * mm});
            skLineSegment(sketch, "E339.3.0.13", {"start": v(-29275, 1700) * mm, "end": v(-28025, 1700) * mm});
            skLineSegment(sketch, "E339.3.0.14", {"start": v(-29950, 2800) * mm, "end": v(-29350, 2800) * mm});
            skLineSegment(sketch, "E339.3.0.15", {"start": v(-29275, 2800) * mm, "end": v(-28025, 2800) * mm});
            skLineSegment(sketch, "E339.3.0.16", {"start": v(-29275, 2800) * mm, "end": v(-29275, 1700) * mm});
            skLineSegment(sketch, "E339.4.0.0", {"start": v(-25650, 1650) * mm, "end": v(-25650, 2850) * mm, "construction": true});
            skLineSegment(sketch, "E339.4.0.1", {"start": v(-24350, 2800) * mm, "end": v(-24950, 2800) * mm});
            skLineSegment(sketch, "E339.4.0.2", {"start": v(-24350, 1700) * mm, "end": v(-24950, 1700) * mm});
            skLineSegment(sketch, "E339.4.0.3", {"start": v(-24350, 2800) * mm, "end": v(-24350, 1700) * mm});
            skLineSegment(sketch, "E339.4.0.4", {"start": v(-24950, 2800) * mm, "end": v(-24950, 1700) * mm});
            skLineSegment(sketch, "E339.4.0.5", {"start": v(-27000, 2850) * mm, "end": v(-27000, 1650) * mm});
            skLineSegment(sketch, "E339.4.0.6", {"start": v(-27000, 1650) * mm, "end": v(-24300, 1650) * mm});
            skLineSegment(sketch, "E339.4.0.7", {"start": v(-25025, 2800) * mm, "end": v(-25025, 1700) * mm});
            skLineSegment(sketch, "E339.4.0.8", {"start": v(-24300, 1650) * mm, "end": v(-24300, 2850) * mm});
            skLineSegment(sketch, "E339.4.0.9", {"start": v(-24300, 2850) * mm, "end": v(-27000, 2850) * mm});
            skLineSegment(sketch, "E339.4.0.10", {"start": v(-26350, 2800) * mm, "end": v(-26350, 1700) * mm});
            skLineSegment(sketch, "E339.4.0.11", {"start": v(-26950, 2800) * mm, "end": v(-26950, 1700) * mm});
            skLineSegment(sketch, "E339.4.0.12", {"start": v(-26950, 1700) * mm, "end": v(-26350, 1700) * mm});
            skLineSegment(sketch, "E339.4.0.13", {"start": v(-26275, 1700) * mm, "end": v(-25025, 1700) * mm});
            skLineSegment(sketch, "E339.4.0.14", {"start": v(-26950, 2800) * mm, "end": v(-26350, 2800) * mm});
            skLineSegment(sketch, "E339.4.0.15", {"start": v(-26275, 2800) * mm, "end": v(-25025, 2800) * mm});
            skLineSegment(sketch, "E339.4.0.16", {"start": v(-26275, 2800) * mm, "end": v(-26275, 1700) * mm});
            skLineSegment(sketch, "E339.5.0.0", {"start": v(-22650, 1650) * mm, "end": v(-22650, 2850) * mm, "construction": true});
            skLineSegment(sketch, "E339.5.0.1", {"start": v(-21350, 2800) * mm, "end": v(-21950, 2800) * mm});
            skLineSegment(sketch, "E339.5.0.2", {"start": v(-21350, 1700) * mm, "end": v(-21950, 1700) * mm});
            skLineSegment(sketch, "E339.5.0.3", {"start": v(-21350, 2800) * mm, "end": v(-21350, 1700) * mm});
            skLineSegment(sketch, "E339.5.0.4", {"start": v(-21950, 2800) * mm, "end": v(-21950, 1700) * mm});
            skLineSegment(sketch, "E339.5.0.5", {"start": v(-24000, 2850) * mm, "end": v(-24000, 1650) * mm});
            skLineSegment(sketch, "E339.5.0.6", {"start": v(-24000, 1650) * mm, "end": v(-21300, 1650) * mm});
            skLineSegment(sketch, "E339.5.0.7", {"start": v(-22025, 2800) * mm, "end": v(-22025, 1700) * mm});
            skLineSegment(sketch, "E339.5.0.8", {"start": v(-21300, 1650) * mm, "end": v(-21300, 2850) * mm});
            skLineSegment(sketch, "E339.5.0.9", {"start": v(-21300, 2850) * mm, "end": v(-24000, 2850) * mm});
            skLineSegment(sketch, "E339.5.0.10", {"start": v(-23350, 2800) * mm, "end": v(-23350, 1700) * mm});
            skLineSegment(sketch, "E339.5.0.11", {"start": v(-23950, 2800) * mm, "end": v(-23950, 1700) * mm});
            skLineSegment(sketch, "E339.5.0.12", {"start": v(-23950, 1700) * mm, "end": v(-23350, 1700) * mm});
            skLineSegment(sketch, "E339.5.0.13", {"start": v(-23275, 1700) * mm, "end": v(-22025, 1700) * mm});
            skLineSegment(sketch, "E339.5.0.14", {"start": v(-23950, 2800) * mm, "end": v(-23350, 2800) * mm});
            skLineSegment(sketch, "E339.5.0.15", {"start": v(-23275, 2800) * mm, "end": v(-22025, 2800) * mm});
            skLineSegment(sketch, "E339.5.0.16", {"start": v(-23275, 2800) * mm, "end": v(-23275, 1700) * mm});
            skLineSegment(sketch, "E339.direction1", {"start": v(-39000, 1650) * mm, "end": v(-36000, 1650) * mm, "construction": true});
            skLineSegment(sketch, "E340", {"start": v(-19625, 0) * mm, "end": v(-19625, 2206.83) * mm, "construction": true});
            skLineSegment(sketch, "E341.MirrorCS", {"start": v(-9300, 2800) * mm, "end": v(-9900, 2800) * mm});
            skLineSegment(sketch, "E342.MirrorCS", {"start": v(-6300, 2800) * mm, "end": v(-6900, 2800) * mm});
            skLineSegment(sketch, "E343.MirrorCS", {"start": v(-8900, 2800) * mm, "end": v(-8300, 2800) * mm});
            skLineSegment(sketch, "E344.MirrorCS", {"start": v(-3300, 2800) * mm, "end": v(-3900, 2800) * mm});
            skLineSegment(sketch, "E345.MirrorCS", {"start": v(-300, 2800) * mm, "end": v(-900, 2800) * mm});
            skLineSegment(sketch, "E346.MirrorCS", {"start": v(-11900, 2800) * mm, "end": v(-11300, 2800) * mm});
            skLineSegment(sketch, "E347.MirrorCS", {"start": v(-5900, 2800) * mm, "end": v(-5300, 2800) * mm});
            skLineSegment(sketch, "E348.MirrorCS", {"start": v(-15300, 1700) * mm, "end": v(-15900, 1700) * mm});
            skLineSegment(sketch, "E349.MirrorCS", {"start": v(-17900, 1700) * mm, "end": v(-17300, 1700) * mm});
            skLineSegment(sketch, "E350.MirrorCS", {"start": v(-12300, 1700) * mm, "end": v(-12900, 1700) * mm});
            skLineSegment(sketch, "E351.MirrorCS", {"start": v(-250, 1650) * mm, "end": v(-2950, 1650) * mm});
            skLineSegment(sketch, "E352.MirrorCS", {"start": v(-2900, 2800) * mm, "end": v(-2300, 2800) * mm});
            skLineSegment(sketch, "E353.MirrorCS", {"start": v(-2900, 1700) * mm, "end": v(-2300, 1700) * mm});
            skLineSegment(sketch, "E354.MirrorCS", {"start": v(-9300, 1700) * mm, "end": v(-9900, 1700) * mm});
            skLineSegment(sketch, "E355.MirrorCS", {"start": v(-14900, 1700) * mm, "end": v(-14300, 1700) * mm});
            skLineSegment(sketch, "E356.MirrorCS", {"start": v(-17900, 2800) * mm, "end": v(-17300, 2800) * mm});
            skLineSegment(sketch, "E357.MirrorCS", {"start": v(-300, 1700) * mm, "end": v(-900, 1700) * mm});
            skLineSegment(sketch, "E358.MirrorCS", {"start": v(-975, 2800) * mm, "end": v(-2225, 2800) * mm});
            skLineSegment(sketch, "E359.MirrorCS", {"start": v(-14900, 2800) * mm, "end": v(-14300, 2800) * mm});
            skLineSegment(sketch, "E360.MirrorCS", {"start": v(-6300, 1700) * mm, "end": v(-6900, 1700) * mm});
            skLineSegment(sketch, "E361.MirrorCS", {"start": v(-11900, 1700) * mm, "end": v(-11300, 1700) * mm});
            skLineSegment(sketch, "E362.MirrorCS", {"start": v(-8950, 2850) * mm, "end": v(-6250, 2850) * mm});
            skLineSegment(sketch, "E363.MirrorCS", {"start": v(-15975, 2800) * mm, "end": v(-17225, 2800) * mm});
            skLineSegment(sketch, "E364.MirrorCS", {"start": v(-3300, 1700) * mm, "end": v(-3900, 1700) * mm});
            skLineSegment(sketch, "E365.MirrorCS", {"start": v(-8900, 1700) * mm, "end": v(-8300, 1700) * mm});
            skLineSegment(sketch, "E366.MirrorCS", {"start": v(-5950, 2850) * mm, "end": v(-3250, 2850) * mm});
            skLineSegment(sketch, "E367.MirrorCS", {"start": v(-15300, 2800) * mm, "end": v(-15900, 2800) * mm});
            skLineSegment(sketch, "E368.MirrorCS", {"start": v(-5900, 1700) * mm, "end": v(-5300, 1700) * mm});
            skLineSegment(sketch, "E369.MirrorCS", {"start": v(-12300, 2800) * mm, "end": v(-12900, 2800) * mm});
            skLineSegment(sketch, "E370.MirrorCS", {"start": v(-9975, 2800) * mm, "end": v(-11225, 2800) * mm});
            skLineSegment(sketch, "E371.MirrorCS", {"start": v(-12975, 2800) * mm, "end": v(-14225, 2800) * mm});
            skLineSegment(sketch, "E372.MirrorCS", {"start": v(-17900, 2800) * mm, "end": v(-17900, 1700) * mm});
            skLineSegment(sketch, "E373.MirrorCS", {"start": v(-12975, 1700) * mm, "end": v(-14225, 1700) * mm});
            skLineSegment(sketch, "E374.MirrorCS", {"start": v(-6975, 2800) * mm, "end": v(-8225, 2800) * mm});
            skLineSegment(sketch, "E375.MirrorCS", {"start": v(-3250, 1650) * mm, "end": v(-5950, 1650) * mm});
            skLineSegment(sketch, "E376.MirrorCS", {"start": v(-9975, 1700) * mm, "end": v(-11225, 1700) * mm});
            skLineSegment(sketch, "E377.MirrorCS", {"start": v(-3975, 2800) * mm, "end": v(-5225, 2800) * mm});
            skLineSegment(sketch, "E378.MirrorCS", {"start": v(-2950, 2850) * mm, "end": v(-250, 2850) * mm});
            skLineSegment(sketch, "E379.MirrorCS", {"start": v(-250, 2850) * mm, "end": v(-250, 1650) * mm});
            skLineSegment(sketch, "E380.MirrorCS", {"start": v(-250, 1650) * mm, "end": v(-3250, 1650) * mm, "construction": true});
            skLineSegment(sketch, "E381.MirrorCS", {"start": v(-6975, 1700) * mm, "end": v(-8225, 1700) * mm});
            skLineSegment(sketch, "E382.MirrorCS", {"start": v(-300, 2800) * mm, "end": v(-300, 1700) * mm});
            skLineSegment(sketch, "E383.MirrorCS", {"start": v(-11950, 2850) * mm, "end": v(-9250, 2850) * mm});
            skLineSegment(sketch, "E384.MirrorCS", {"start": v(-975, 1700) * mm, "end": v(-2225, 1700) * mm});
            skLineSegment(sketch, "E385.MirrorCS", {"start": v(-17950, 2850) * mm, "end": v(-15250, 2850) * mm});
            skLineSegment(sketch, "E386.MirrorCS", {"start": v(-3975, 1700) * mm, "end": v(-5225, 1700) * mm});
            skLineSegment(sketch, "E387.MirrorCS", {"start": v(-11950, 1650) * mm, "end": v(-11950, 2850) * mm});
            skLineSegment(sketch, "E388.MirrorCS", {"start": v(-15250, 1650) * mm, "end": v(-17950, 1650) * mm});
            skLineSegment(sketch, "E389.MirrorCS", {"start": v(-14950, 2850) * mm, "end": v(-12250, 2850) * mm});
            skLineSegment(sketch, "E390.MirrorCS", {"start": v(-6300, 2800) * mm, "end": v(-6300, 1700) * mm});
            skLineSegment(sketch, "E391.MirrorCS", {"start": v(-8950, 1650) * mm, "end": v(-8950, 2850) * mm});
            skLineSegment(sketch, "E392.MirrorCS", {"start": v(-12250, 1650) * mm, "end": v(-14950, 1650) * mm});
            skLineSegment(sketch, "E393.MirrorCS", {"start": v(-9250, 2850) * mm, "end": v(-9250, 1650) * mm});
            skLineSegment(sketch, "E394.MirrorCS", {"start": v(-6250, 1650) * mm, "end": v(-8950, 1650) * mm});
            skLineSegment(sketch, "E395.MirrorCS", {"start": v(-9975, 2800) * mm, "end": v(-9975, 1700) * mm});
            skLineSegment(sketch, "E396.MirrorCS", {"start": v(-6975, 2800) * mm, "end": v(-6975, 1700) * mm});
            skLineSegment(sketch, "E397.MirrorCS", {"start": v(-8225, 2800) * mm, "end": v(-8225, 1700) * mm});
            skLineSegment(sketch, "E398.MirrorCS", {"start": v(-9250, 1650) * mm, "end": v(-11950, 1650) * mm});
            skLineSegment(sketch, "E399.MirrorCS", {"start": v(-15975, 1700) * mm, "end": v(-17225, 1700) * mm});
            skLineSegment(sketch, "E400.MirrorCS", {"start": v(-5225, 2800) * mm, "end": v(-5225, 1700) * mm});
            skLineSegment(sketch, "E401.MirrorCS", {"start": v(-14300, 2800) * mm, "end": v(-14300, 1700) * mm});
            skLineSegment(sketch, "E402.MirrorCS", {"start": v(-4600, 1650) * mm, "end": v(-4600, 2850) * mm, "construction": true});
            skLineSegment(sketch, "E403.MirrorCS", {"start": v(-3975, 2800) * mm, "end": v(-3975, 1700) * mm});
            skLineSegment(sketch, "E404.MirrorCS", {"start": v(-6250, 2850) * mm, "end": v(-6250, 1650) * mm});
            skLineSegment(sketch, "E405.MirrorCS", {"start": v(-11300, 2800) * mm, "end": v(-11300, 1700) * mm});
            skLineSegment(sketch, "E406.MirrorCS", {"start": v(-14900, 2800) * mm, "end": v(-14900, 1700) * mm});
            skLineSegment(sketch, "E407.MirrorCS", {"start": v(-15300, 2800) * mm, "end": v(-15300, 1700) * mm});
            skLineSegment(sketch, "E408.MirrorCS", {"start": v(-2225, 2800) * mm, "end": v(-2225, 1700) * mm});
            skLineSegment(sketch, "E409.MirrorCS", {"start": v(-2950, 1650) * mm, "end": v(-2950, 2850) * mm});
            skLineSegment(sketch, "E410.MirrorCS", {"start": v(-12300, 2800) * mm, "end": v(-12300, 1700) * mm});
            skLineSegment(sketch, "E411.MirrorCS", {"start": v(-15900, 2800) * mm, "end": v(-15900, 1700) * mm});
            skLineSegment(sketch, "E412.MirrorCS", {"start": v(-3250, 2850) * mm, "end": v(-3250, 1650) * mm});
            skLineSegment(sketch, "E413.MirrorCS", {"start": v(-8300, 2800) * mm, "end": v(-8300, 1700) * mm});
            skLineSegment(sketch, "E414.MirrorCS", {"start": v(-2900, 2800) * mm, "end": v(-2900, 1700) * mm});
            skLineSegment(sketch, "E415.MirrorCS", {"start": v(-11900, 2800) * mm, "end": v(-11900, 1700) * mm});
            skLineSegment(sketch, "E416.MirrorCS", {"start": v(-2300, 2800) * mm, "end": v(-2300, 1700) * mm});
            skLineSegment(sketch, "E417.MirrorCS", {"start": v(-1600, 1650) * mm, "end": v(-1600, 2850) * mm, "construction": true});
            skLineSegment(sketch, "E418.MirrorCS", {"start": v(-900, 2800) * mm, "end": v(-900, 1700) * mm});
            skLineSegment(sketch, "E419.MirrorCS", {"start": v(-6900, 2800) * mm, "end": v(-6900, 1700) * mm});
            skLineSegment(sketch, "E420.MirrorCS", {"start": v(-14950, 1650) * mm, "end": v(-14950, 2850) * mm});
            skLineSegment(sketch, "E421.MirrorCS", {"start": v(-17225, 2800) * mm, "end": v(-17225, 1700) * mm});
            skLineSegment(sketch, "E422.MirrorCS", {"start": v(-3300, 2800) * mm, "end": v(-3300, 1700) * mm});
            skLineSegment(sketch, "E423.MirrorCS", {"start": v(-975, 2800) * mm, "end": v(-975, 1700) * mm});
            skLineSegment(sketch, "E424.MirrorCS", {"start": v(-9300, 2800) * mm, "end": v(-9300, 1700) * mm});
            skLineSegment(sketch, "E425.MirrorCS", {"start": v(-12900, 2800) * mm, "end": v(-12900, 1700) * mm});
            skLineSegment(sketch, "E426.MirrorCS", {"start": v(-16600, 1650) * mm, "end": v(-16600, 2850) * mm, "construction": true});
            skLineSegment(sketch, "E427.MirrorCS", {"start": v(-15975, 2800) * mm, "end": v(-15975, 1700) * mm});
            skLineSegment(sketch, "E428.MirrorCS", {"start": v(-5300, 2800) * mm, "end": v(-5300, 1700) * mm});
            skLineSegment(sketch, "E429.MirrorCS", {"start": v(-8900, 2800) * mm, "end": v(-8900, 1700) * mm});
            skLineSegment(sketch, "E430.MirrorCS", {"start": v(-14225, 2800) * mm, "end": v(-14225, 1700) * mm});
            skLineSegment(sketch, "E431.MirrorCS", {"start": v(-3900, 2800) * mm, "end": v(-3900, 1700) * mm});
            skLineSegment(sketch, "E432.MirrorCS", {"start": v(-13600, 1650) * mm, "end": v(-13600, 2850) * mm, "construction": true});
            skLineSegment(sketch, "E433.MirrorCS", {"start": v(-9900, 2800) * mm, "end": v(-9900, 1700) * mm});
            skLineSegment(sketch, "E434.MirrorCS", {"start": v(-12975, 2800) * mm, "end": v(-12975, 1700) * mm});
            skLineSegment(sketch, "E435.MirrorCS", {"start": v(-17950, 1650) * mm, "end": v(-17950, 2850) * mm});
            skLineSegment(sketch, "E436.MirrorCS", {"start": v(-5900, 2800) * mm, "end": v(-5900, 1700) * mm});
            skLineSegment(sketch, "E437.MirrorCS", {"start": v(-11225, 2800) * mm, "end": v(-11225, 1700) * mm});
            skLineSegment(sketch, "E438.MirrorCS", {"start": v(-15250, 2850) * mm, "end": v(-15250, 1650) * mm});
            skLineSegment(sketch, "E439.MirrorCS", {"start": v(-7600, 1650) * mm, "end": v(-7600, 2850) * mm, "construction": true});
            skLineSegment(sketch, "E440.MirrorCS", {"start": v(-10600, 1650) * mm, "end": v(-10600, 2850) * mm, "construction": true});
            skLineSegment(sketch, "E441.MirrorCS", {"start": v(-12250, 2850) * mm, "end": v(-12250, 1650) * mm});
            skLineSegment(sketch, "E442.MirrorCS", {"start": v(-17300, 2800) * mm, "end": v(-17300, 1700) * mm});
            skLineSegment(sketch, "E443.MirrorCS", {"start": v(-5950, 1650) * mm, "end": v(-5950, 2850) * mm});
            skLineSegment(sketch, "E444.0.6.0", {"start": v(-19650, 1650) * mm, "end": v(-19650, 2850) * mm, "construction": true});
            skLineSegment(sketch, "E444.3.6.0", {"start": v(-18350, 2800) * mm, "end": v(-18950, 2800) * mm});
            skLineSegment(sketch, "E444.6.6.0", {"start": v(-18350, 1700) * mm, "end": v(-18950, 1700) * mm});
            skLineSegment(sketch, "E444.9.6.0", {"start": v(-18350, 2800) * mm, "end": v(-18350, 1700) * mm});
            skLineSegment(sketch, "E444.12.6.0", {"start": v(-18950, 2800) * mm, "end": v(-18950, 1700) * mm});
            skLineSegment(sketch, "E444.15.6.0", {"start": v(-21000, 2850) * mm, "end": v(-21000, 1650) * mm});
            skLineSegment(sketch, "E444.18.6.0", {"start": v(-21000, 1650) * mm, "end": v(-18300, 1650) * mm});
            skLineSegment(sketch, "E444.21.6.0", {"start": v(-19025, 2800) * mm, "end": v(-19025, 1700) * mm});
            skLineSegment(sketch, "E444.24.6.0", {"start": v(-18300, 1650) * mm, "end": v(-18300, 2850) * mm});
            skLineSegment(sketch, "E444.27.6.0", {"start": v(-18300, 2850) * mm, "end": v(-21000, 2850) * mm});
            skLineSegment(sketch, "E444.30.6.0", {"start": v(-20350, 2800) * mm, "end": v(-20350, 1700) * mm});
            skLineSegment(sketch, "E444.33.6.0", {"start": v(-20950, 2800) * mm, "end": v(-20950, 1700) * mm});
            skLineSegment(sketch, "E444.36.6.0", {"start": v(-20950, 1700) * mm, "end": v(-20350, 1700) * mm});
            skLineSegment(sketch, "E444.39.6.0", {"start": v(-20275, 1700) * mm, "end": v(-19025, 1700) * mm});
            skLineSegment(sketch, "E444.42.6.0", {"start": v(-20950, 2800) * mm, "end": v(-20350, 2800) * mm});
            skLineSegment(sketch, "E444.45.6.0", {"start": v(-20275, 2800) * mm, "end": v(-19025, 2800) * mm});
            skLineSegment(sketch, "E444.48.6.0", {"start": v(-20275, 2800) * mm, "end": v(-20275, 1700) * mm});
            skSolve(sketch);
        }
        {
            var Q0;
            Q0=qSketchRegion(id+"F14",true);
            extrude(context, id + "F15", {"entities" : qUnion([Q0]), "depth" : 50 * mm, "offsetDistance" : 25 * mm});
        }
        {
            var Q0;
            Q0=makeQuery(id+"F3.boolean.opBoolean","MERGE",FACE,{"derivedFrom":[makeQuery(id+"F1.opExtrude","SWEPT_FACE",FACE,{"disambiguationData":[OSD([sQuery(id+"F0.wireOp",EDGE,"E0.left")])]}),makeQuery(id+"F3.opExtrude","SWEPT_FACE",FACE,{"disambiguationData":[OSD([sQuery(id+"F2.wireOp",EDGE,"E1.0.0")])]})]});
            var sketch = newSketch(context, id + "F16", { "sketchPlane" : qUnion([Q0])});
            skLineSegment(sketch, "E445", {"start": v(9250, 150) * mm, "end": v(11050, 150) * mm});
            skLineSegment(sketch, "E446", {"start": v(11050, 0) * mm, "end": v(9250, 0) * mm});
            skLineSegment(sketch, "E447", {"start": v(9250, 0) * mm, "end": v(9250, 150) * mm});
            skLineSegment(sketch, "E448", {"start": v(11050, 150) * mm, "end": v(11050, 0) * mm});
            skSolve(sketch);
        }
        {
            var Q0;
            Q0=qSketchRegion(id+"F16",true);
            extrude(context, id + "F17", {"entities" : qUnion([Q0]), "operationType" : NewBodyOperationType.ADD, "oppositeDirection" : true, "depth" : 3200 * mm, "offsetDistance" : 25 * mm});
        }
        {
            var Q0;
            Q0=makeQuery(id+"F3.boolean.opBoolean","MERGE",FACE,{"derivedFrom":[makeQuery(id+"F1.opExtrude","SWEPT_FACE",FACE,{"disambiguationData":[OSD([sQuery(id+"F0.wireOp",EDGE,"E0.right")])]}),makeQuery(id+"F3.opExtrude","SWEPT_FACE",FACE,{"disambiguationData":[OSD([sQuery(id+"F2.wireOp",EDGE,"E1.0.2")])]})]});
            var sketch = newSketch(context, id + "F18", { "sketchPlane" : qUnion([Q0])});
            skLineSegment(sketch, "E449.0", {"start": v(-9250, 150) * mm, "end": v(-11050, 150) * mm});
            skLineSegment(sketch, "E449.11", {"start": v(-11050, 0) * mm, "end": v(-9250, 0) * mm});
            skLineSegment(sketch, "E449.12", {"start": v(-9250, 0) * mm, "end": v(-9250, 150) * mm});
            skLineSegment(sketch, "E450", {"start": v(-11050, 150) * mm, "end": v(-11050, 0) * mm});
            skSolve(sketch);
        }
        {
            var Q0;
            Q0=qSketchRegion(id+"F18",true);
            extrude(context, id + "F19", {"entities" : qUnion([Q0]), "operationType" : NewBodyOperationType.ADD, "oppositeDirection" : true, "depth" : 3200 * mm, "offsetDistance" : 25 * mm});
        }
        {
            var Q0;
            Q0=makeQuery(id+"F19.boolean.opBoolean","MERGE",FACE,{"derivedFrom":[makeQuery(id+"FsX6fwVixHOvQLt_53.boolean.opBoolean","MERGE",FACE,{"derivedFrom":[makeQuery(id+"F17.boolean.opBoolean","MERGE",FACE,{"derivedFrom":[makeQuery(id+"F5.boolean.opBoolean","MERGE",FACE,{"derivedFrom":[makeQuery(id+"F1.opExtrude","CAP_FACE",FACE,{"disambiguationData":[OSD([sQuery(id+"F0.wireOp",EDGE,"E0.bottom"),sQuery(id+"F0.wireOp",EDGE,"E0.top"),sQuery(id+"F0.wireOp",EDGE,"E0.left"),sQuery(id+"F0.wireOp",EDGE,"E0.right")])],"isStart":false}),makeQuery(id+"F5.opExtrude","SWEPT_FACE",FACE,{"disambiguationData":[OSD([sQuery(id+"F4.wireOp",EDGE,"E3")])]}),makeQuery(id+"F5.opExtrude","SWEPT_FACE",FACE,{"disambiguationData":[OSD([sQuery(id+"F4.wireOp",EDGE,"E11")])]}),makeQuery(id+"F5.opExtrude","SWEPT_FACE",FACE,{"disambiguationData":[OSD([sQuery(id+"F4.wireOp",EDGE,"E17.bottom")])]}),makeQuery(id+"F5.opExtrude","SWEPT_FACE",FACE,{"disambiguationData":[OSD([sQuery(id+"F4.wireOp",EDGE,"E31.MirrorCS")])]}),makeQuery(id+"F5.opExtrude","SWEPT_FACE",FACE,{"disambiguationData":[OSD([sQuery(id+"F4.wireOp",EDGE,"E34.MirrorCS")])]})]}),makeQuery(id+"F17.opExtrude","SWEPT_FACE",FACE,{"disambiguationData":[OSD([sQuery(id+"F16.wireOp",EDGE,"E445")])]})]}),makeQuery(id+"FsX6fwVixHOvQLt_53.opExtrude","SWEPT_FACE",FACE,{"disambiguationData":[OSD([sQuery(id+"F5VrGisfebLuhc7_53.wireOp",EDGE,"022de531-5e36-4a2e-b47e-72a6ce5d027f.0")])]})]}),makeQuery(id+"F19.opExtrude","SWEPT_FACE",FACE,{"disambiguationData":[OSD([sQuery(id+"F18.wireOp",EDGE,"E449.0")])]})]});
            var sketch = newSketch(context, id + "F20", { "sketchPlane" : qUnion([Q0])});
            skLineSegment(sketch, "E451.bottom", {"start": v(3200, -9250) * mm, "end": v(18250, -9250) * mm});
            skLineSegment(sketch, "E451.top", {"start": v(3200, -11050) * mm, "end": v(18250, -11050) * mm});
            skLineSegment(sketch, "E451.left", {"start": v(3200, -9250) * mm, "end": v(3200, -11050) * mm});
            skLineSegment(sketch, "E451.right", {"start": v(18250, -9250) * mm, "end": v(18250, -11050) * mm});
            skLineSegment(sketch, "E452.bottom", {"start": v(20950, -9250) * mm, "end": v(36050, -9250) * mm});
            skLineSegment(sketch, "E452.top", {"start": v(20950, -11050) * mm, "end": v(36050, -11050) * mm});
            skLineSegment(sketch, "E452.left", {"start": v(20950, -9250) * mm, "end": v(20950, -11050) * mm});
            skLineSegment(sketch, "E452.right", {"start": v(36050, -9250) * mm, "end": v(36050, -11050) * mm});
            skSolve(sketch);
        }
        {
            var Q0;
            Q0=qSketchRegion(id+"F20",true);
            var Q1;
            Q1=makeQuery(id+"F17.opExtrude","SWEPT_FACE",FACE,{"disambiguationData":[OSD([sQuery(id+"F16.wireOp",EDGE,"E446")])]});
            extrude(context, id + "F21", {"entities" : qUnion([Q0]), "operationType" : NewBodyOperationType.ADD, "endBound" : BoundingType.UP_TO_SURFACE, "oppositeDirection" : true, "depth" : 25 * mm, "endBoundEntityFace" : qUnion([Q1]), "offsetDistance" : 25 * mm});
        }
        {
            var Q0;
            Q0=makeQuery(id+"F21.boolean.opBoolean","MERGE",FACE,{"derivedFrom":[makeQuery(id+"F19.boolean.opBoolean","MERGE",FACE,{"derivedFrom":[makeQuery(id+"FsX6fwVixHOvQLt_53.boolean.opBoolean","MERGE",FACE,{"derivedFrom":[makeQuery(id+"F17.boolean.opBoolean","MERGE",FACE,{"derivedFrom":[makeQuery(id+"F5.boolean.opBoolean","MERGE",FACE,{"derivedFrom":[makeQuery(id+"F1.opExtrude","CAP_FACE",FACE,{"disambiguationData":[OSD([sQuery(id+"F0.wireOp",EDGE,"E0.bottom"),sQuery(id+"F0.wireOp",EDGE,"E0.top"),sQuery(id+"F0.wireOp",EDGE,"E0.left"),sQuery(id+"F0.wireOp",EDGE,"E0.right")])],"isStart":false}),makeQuery(id+"F5.opExtrude","SWEPT_FACE",FACE,{"disambiguationData":[OSD([sQuery(id+"F4.wireOp",EDGE,"E3")])]}),makeQuery(id+"F5.opExtrude","SWEPT_FACE",FACE,{"disambiguationData":[OSD([sQuery(id+"F4.wireOp",EDGE,"E11")])]}),makeQuery(id+"F5.opExtrude","SWEPT_FACE",FACE,{"disambiguationData":[OSD([sQuery(id+"F4.wireOp",EDGE,"E17.bottom")])]}),makeQuery(id+"F5.opExtrude","SWEPT_FACE",FACE,{"disambiguationData":[OSD([sQuery(id+"F4.wireOp",EDGE,"E31.MirrorCS")])]}),makeQuery(id+"F5.opExtrude","SWEPT_FACE",FACE,{"disambiguationData":[OSD([sQuery(id+"F4.wireOp",EDGE,"E34.MirrorCS")])]})]}),makeQuery(id+"F17.opExtrude","SWEPT_FACE",FACE,{"disambiguationData":[OSD([sQuery(id+"F16.wireOp",EDGE,"E445")])]})]}),makeQuery(id+"FsX6fwVixHOvQLt_53.opExtrude","SWEPT_FACE",FACE,{"disambiguationData":[OSD([sQuery(id+"F5VrGisfebLuhc7_53.wireOp",EDGE,"022de531-5e36-4a2e-b47e-72a6ce5d027f.0")])]})]}),makeQuery(id+"F19.opExtrude","SWEPT_FACE",FACE,{"disambiguationData":[OSD([sQuery(id+"F18.wireOp",EDGE,"E449.0")])]})]}),makeQuery(id+"F21.opExtrude","CAP_FACE",FACE,{"disambiguationData":[OSD([sQuery(id+"F20.wireOp",EDGE,"E451.bottom"),sQuery(id+"F20.wireOp",EDGE,"E451.top"),sQuery(id+"F20.wireOp",EDGE,"E451.left"),sQuery(id+"F20.wireOp",EDGE,"E451.right")])],"isStart":true}),makeQuery(id+"F21.opExtrude","CAP_FACE",FACE,{"disambiguationData":[OSD([sQuery(id+"F20.wireOp",EDGE,"E452.bottom"),sQuery(id+"F20.wireOp",EDGE,"E452.top"),sQuery(id+"F20.wireOp",EDGE,"E452.left"),sQuery(id+"F20.wireOp",EDGE,"E452.right")])],"isStart":true})]});
            var sketch = newSketch(context, id + "F22", { "sketchPlane" : qUnion([Q0])});
            skLineSegment(sketch, "E453.bottom", {"start": v(0, -9250) * mm, "end": v(100, -9250) * mm});
            skLineSegment(sketch, "E453.top", {"start": v(0, -11050) * mm, "end": v(100, -11050) * mm});
            skLineSegment(sketch, "E453.left", {"start": v(0, -9250) * mm, "end": v(0, -11050) * mm});
            skLineSegment(sketch, "E453.right", {"start": v(100, -9250) * mm, "end": v(100, -10950) * mm});
            skLineSegment(sketch, "E454.bottom", {"start": v(100, -11050) * mm, "end": v(18250, -11050) * mm});
            skLineSegment(sketch, "E454.top", {"start": v(100, -10950) * mm, "end": v(18150, -10950) * mm});
            skLineSegment(sketch, "E454.right", {"start": v(18250, -11050) * mm, "end": v(18250, -10950) * mm});
            skLineSegment(sketch, "E455.top", {"start": v(18250, -9250) * mm, "end": v(18150, -9250) * mm});
            skLineSegment(sketch, "E455.left", {"start": v(18250, -10950) * mm, "end": v(18250, -9250) * mm});
            skLineSegment(sketch, "E455.right", {"start": v(18150, -10950) * mm, "end": v(18150, -9250) * mm});
            skLineSegment(sketch, "E456.bottom", {"start": v(39250, -9250) * mm, "end": v(39150, -9250) * mm});
            skLineSegment(sketch, "E456.top", {"start": v(39250, -11050) * mm, "end": v(39150, -11050) * mm});
            skLineSegment(sketch, "E456.left", {"start": v(39250, -9250) * mm, "end": v(39250, -11050) * mm});
            skLineSegment(sketch, "E456.right", {"start": v(39150, -9250) * mm, "end": v(39150, -10950) * mm});
            skLineSegment(sketch, "E457.bottom", {"start": v(39150, -11050) * mm, "end": v(20950, -11050) * mm});
            skLineSegment(sketch, "E457.top", {"start": v(39150, -10950) * mm, "end": v(21050, -10950) * mm});
            skLineSegment(sketch, "E457.right", {"start": v(20950, -11050) * mm, "end": v(20950, -10950) * mm});
            skLineSegment(sketch, "E458.top", {"start": v(20950, -9250) * mm, "end": v(21050, -9250) * mm});
            skLineSegment(sketch, "E458.left", {"start": v(20950, -10950) * mm, "end": v(20950, -9250) * mm});
            skLineSegment(sketch, "E458.right", {"start": v(21050, -10950) * mm, "end": v(21050, -9250) * mm});
            skSolve(sketch);
        }
        {
            var Q0;
            Q0=qSketchRegion(id+"F22",true);
            extrude(context, id + "F23", {"entities" : qUnion([Q0]), "operationType" : NewBodyOperationType.ADD, "depth" : 600 * mm, "offsetDistance" : 25 * mm});
        }
        {
            var Q0;
            Q0=makeQuery(id+"F23.opExtrude","CAP_FACE",FACE,{"disambiguationData":[OSD([sQuery(id+"F22.wireOp",EDGE,"E453.bottom"),sQuery(id+"F22.wireOp",EDGE,"E453.top"),sQuery(id+"F22.wireOp",EDGE,"E453.left"),sQuery(id+"F22.wireOp",EDGE,"E453.right")])],"isStart":false});
            var sketch = newSketch(context, id + "F24", { "sketchPlane" : qUnion([Q0])});
            skLineSegment(sketch, "E459.bottom", {"start": v(0, -9250) * mm, "end": v(50, -9250) * mm});
            skLineSegment(sketch, "E459.top", {"start": v(0, -9300) * mm, "end": v(50, -9300) * mm});
            skLineSegment(sketch, "E459.left", {"start": v(0, -9250) * mm, "end": v(0, -9300) * mm});
            skLineSegment(sketch, "E459.right", {"start": v(50, -9250) * mm, "end": v(50, -9300) * mm});
            skLineSegment(sketch, "E460.0.1.0", {"start": v(0, -10120) * mm, "end": v(50, -10120) * mm});
            skLineSegment(sketch, "E460.0.1.1", {"start": v(0, -10170) * mm, "end": v(50, -10170) * mm});
            skLineSegment(sketch, "E460.0.1.2", {"start": v(0, -10120) * mm, "end": v(0, -10170) * mm});
            skLineSegment(sketch, "E460.0.1.3", {"start": v(50, -10120) * mm, "end": v(50, -10170) * mm});
            skLineSegment(sketch, "E460.0.2.0", {"start": v(0, -10990) * mm, "end": v(50, -10990) * mm});
            skLineSegment(sketch, "E460.0.2.1", {"start": v(0, -11040) * mm, "end": v(50, -11040) * mm});
            skLineSegment(sketch, "E460.0.2.2", {"start": v(0, -10990) * mm, "end": v(0, -11040) * mm});
            skLineSegment(sketch, "E460.0.2.3", {"start": v(50, -10990) * mm, "end": v(50, -11040) * mm});
            skLineSegment(sketch, "E460.direction1", {"start": v(0, -9300) * mm, "end": v(25, -9300) * mm, "construction": true});
            skLineSegment(sketch, "E460.direction2", {"start": v(0, -9300) * mm, "end": v(0, -10170) * mm, "construction": true});
            skLineSegment(sketch, "E461.MirrorCS", {"start": v(39250, -9250) * mm, "end": v(39250, -9300) * mm});
            skLineSegment(sketch, "E462.MirrorCS", {"start": v(39250, -9300) * mm, "end": v(39225, -9300) * mm, "construction": true});
            skLineSegment(sketch, "E463.MirrorCS", {"start": v(39200, -9250) * mm, "end": v(39200, -9300) * mm});
            skLineSegment(sketch, "E464.MirrorCS", {"start": v(39250, -9300) * mm, "end": v(39200, -9300) * mm});
            skLineSegment(sketch, "E465.MirrorCS", {"start": v(39250, -9250) * mm, "end": v(39200, -9250) * mm});
            skLineSegment(sketch, "E466.MirrorCS", {"start": v(39250, -11040) * mm, "end": v(39200, -11040) * mm});
            skLineSegment(sketch, "E467.MirrorCS", {"start": v(39200, -10120) * mm, "end": v(39200, -10170) * mm});
            skLineSegment(sketch, "E468.MirrorCS", {"start": v(39250, -10120) * mm, "end": v(39250, -10170) * mm});
            skLineSegment(sketch, "E469.MirrorCS", {"start": v(39250, -10170) * mm, "end": v(39200, -10170) * mm});
            skLineSegment(sketch, "E470.MirrorCS", {"start": v(39250, -10120) * mm, "end": v(39200, -10120) * mm});
            skLineSegment(sketch, "E471.MirrorCS", {"start": v(39200, -10990) * mm, "end": v(39200, -11040) * mm});
            skLineSegment(sketch, "E472.MirrorCS", {"start": v(39250, -10990) * mm, "end": v(39250, -11040) * mm});
            skLineSegment(sketch, "E473.MirrorCS", {"start": v(39250, -10990) * mm, "end": v(39200, -10990) * mm});
            skLineSegment(sketch, "E474.MirrorCS", {"start": v(39250, -9300) * mm, "end": v(39250, -10170) * mm, "construction": true});
            skPoint(sketch, "E475", {"position": v(18250, -9250) * mm});
            skPoint(sketch, "E476", {"position": v(20950, -9250) * mm});
            skLineSegment(sketch, "E477.bottom", {"start": v(18200, -9250) * mm, "end": v(18250, -9250) * mm});
            skLineSegment(sketch, "E477.top", {"start": v(18200, -9300) * mm, "end": v(18250, -9300) * mm});
            skLineSegment(sketch, "E477.left", {"start": v(18200, -9250) * mm, "end": v(18200, -9300) * mm});
            skLineSegment(sketch, "E477.right", {"start": v(18250, -9250) * mm, "end": v(18250, -9300) * mm});
            skLineSegment(sketch, "E478.0.1.0", {"start": v(18200, -10120) * mm, "end": v(18250, -10120) * mm});
            skLineSegment(sketch, "E478.0.1.1", {"start": v(18200, -10170) * mm, "end": v(18250, -10170) * mm});
            skLineSegment(sketch, "E478.0.1.2", {"start": v(18200, -10120) * mm, "end": v(18200, -10170) * mm});
            skLineSegment(sketch, "E478.0.1.3", {"start": v(18250, -10120) * mm, "end": v(18250, -10170) * mm});
            skLineSegment(sketch, "E478.0.2.0", {"start": v(18200, -10990) * mm, "end": v(18250, -10990) * mm});
            skLineSegment(sketch, "E478.0.2.1", {"start": v(18200, -11040) * mm, "end": v(18250, -11040) * mm});
            skLineSegment(sketch, "E478.0.2.2", {"start": v(18200, -10990) * mm, "end": v(18200, -11040) * mm});
            skLineSegment(sketch, "E478.0.2.3", {"start": v(18250, -10990) * mm, "end": v(18250, -11040) * mm});
            skLineSegment(sketch, "E478.direction1", {"start": v(18200, -9300) * mm, "end": v(18225, -9300) * mm, "construction": true});
            skLineSegment(sketch, "E478.direction2", {"start": v(18200, -9300) * mm, "end": v(18200, -10170) * mm, "construction": true});
            skLineSegment(sketch, "E479.bottom", {"start": v(20950, -9250) * mm, "end": v(21000, -9250) * mm});
            skLineSegment(sketch, "E479.top", {"start": v(20950, -9300) * mm, "end": v(21000, -9300) * mm});
            skLineSegment(sketch, "E479.left", {"start": v(20950, -9250) * mm, "end": v(20950, -9300) * mm});
            skLineSegment(sketch, "E479.right", {"start": v(21000, -9250) * mm, "end": v(21000, -9300) * mm});
            skLineSegment(sketch, "E480.0.1.0", {"start": v(20950, -10120) * mm, "end": v(21000, -10120) * mm});
            skLineSegment(sketch, "E480.0.1.1", {"start": v(20950, -10170) * mm, "end": v(21000, -10170) * mm});
            skLineSegment(sketch, "E480.0.1.2", {"start": v(20950, -10120) * mm, "end": v(20950, -10170) * mm});
            skLineSegment(sketch, "E480.0.1.3", {"start": v(21000, -10120) * mm, "end": v(21000, -10170) * mm});
            skLineSegment(sketch, "E480.0.2.0", {"start": v(20950, -10990) * mm, "end": v(21000, -10990) * mm});
            skLineSegment(sketch, "E480.0.2.1", {"start": v(20950, -11040) * mm, "end": v(21000, -11040) * mm});
            skLineSegment(sketch, "E480.0.2.2", {"start": v(20950, -10990) * mm, "end": v(20950, -11040) * mm});
            skLineSegment(sketch, "E480.0.2.3", {"start": v(21000, -10990) * mm, "end": v(21000, -11040) * mm});
            skLineSegment(sketch, "E480.direction1", {"start": v(20950, -9300) * mm, "end": v(20975, -9300) * mm, "construction": true});
            skLineSegment(sketch, "E480.direction2", {"start": v(20950, -9300) * mm, "end": v(20950, -10170) * mm, "construction": true});
            skLineSegment(sketch, "E481.1.0.0", {"start": v(880, -10990) * mm, "end": v(930, -10990) * mm});
            skLineSegment(sketch, "E481.1.0.1", {"start": v(880, -10990) * mm, "end": v(880, -11040) * mm});
            skLineSegment(sketch, "E481.1.0.2", {"start": v(930, -10990) * mm, "end": v(930, -11040) * mm});
            skLineSegment(sketch, "E481.1.0.3", {"start": v(880, -11040) * mm, "end": v(930, -11040) * mm});
            skLineSegment(sketch, "E481.2.0.0", {"start": v(1760, -10990) * mm, "end": v(1810, -10990) * mm});
            skLineSegment(sketch, "E481.2.0.1", {"start": v(1760, -10990) * mm, "end": v(1760, -11040) * mm});
            skLineSegment(sketch, "E481.2.0.2", {"start": v(1810, -10990) * mm, "end": v(1810, -11040) * mm});
            skLineSegment(sketch, "E481.2.0.3", {"start": v(1760, -11040) * mm, "end": v(1810, -11040) * mm});
            skLineSegment(sketch, "E481.3.0.0", {"start": v(2640, -10990) * mm, "end": v(2690, -10990) * mm});
            skLineSegment(sketch, "E481.3.0.1", {"start": v(2640, -10990) * mm, "end": v(2640, -11040) * mm});
            skLineSegment(sketch, "E481.3.0.2", {"start": v(2690, -10990) * mm, "end": v(2690, -11040) * mm});
            skLineSegment(sketch, "E481.3.0.3", {"start": v(2640, -11040) * mm, "end": v(2690, -11040) * mm});
            skLineSegment(sketch, "E481.4.0.0", {"start": v(3520, -10990) * mm, "end": v(3570, -10990) * mm});
            skLineSegment(sketch, "E481.4.0.1", {"start": v(3520, -10990) * mm, "end": v(3520, -11040) * mm});
            skLineSegment(sketch, "E481.4.0.2", {"start": v(3570, -10990) * mm, "end": v(3570, -11040) * mm});
            skLineSegment(sketch, "E481.4.0.3", {"start": v(3520, -11040) * mm, "end": v(3570, -11040) * mm});
            skLineSegment(sketch, "E481.5.0.0", {"start": v(4400, -10990) * mm, "end": v(4450, -10990) * mm});
            skLineSegment(sketch, "E481.5.0.1", {"start": v(4400, -10990) * mm, "end": v(4400, -11040) * mm});
            skLineSegment(sketch, "E481.5.0.2", {"start": v(4450, -10990) * mm, "end": v(4450, -11040) * mm});
            skLineSegment(sketch, "E481.5.0.3", {"start": v(4400, -11040) * mm, "end": v(4450, -11040) * mm});
            skLineSegment(sketch, "E481.6.0.0", {"start": v(5280, -10990) * mm, "end": v(5330, -10990) * mm});
            skLineSegment(sketch, "E481.6.0.1", {"start": v(5280, -10990) * mm, "end": v(5280, -11040) * mm});
            skLineSegment(sketch, "E481.6.0.2", {"start": v(5330, -10990) * mm, "end": v(5330, -11040) * mm});
            skLineSegment(sketch, "E481.6.0.3", {"start": v(5280, -11040) * mm, "end": v(5330, -11040) * mm});
            skLineSegment(sketch, "E481.7.0.0", {"start": v(6160, -10990) * mm, "end": v(6210, -10990) * mm});
            skLineSegment(sketch, "E481.7.0.1", {"start": v(6160, -10990) * mm, "end": v(6160, -11040) * mm});
            skLineSegment(sketch, "E481.7.0.2", {"start": v(6210, -10990) * mm, "end": v(6210, -11040) * mm});
            skLineSegment(sketch, "E481.7.0.3", {"start": v(6160, -11040) * mm, "end": v(6210, -11040) * mm});
            skLineSegment(sketch, "E481.8.0.0", {"start": v(7040, -10990) * mm, "end": v(7090, -10990) * mm});
            skLineSegment(sketch, "E481.8.0.1", {"start": v(7040, -10990) * mm, "end": v(7040, -11040) * mm});
            skLineSegment(sketch, "E481.8.0.2", {"start": v(7090, -10990) * mm, "end": v(7090, -11040) * mm});
            skLineSegment(sketch, "E481.8.0.3", {"start": v(7040, -11040) * mm, "end": v(7090, -11040) * mm});
            skLineSegment(sketch, "E481.9.0.0", {"start": v(7920, -10990) * mm, "end": v(7970, -10990) * mm});
            skLineSegment(sketch, "E481.9.0.1", {"start": v(7920, -10990) * mm, "end": v(7920, -11040) * mm});
            skLineSegment(sketch, "E481.9.0.2", {"start": v(7970, -10990) * mm, "end": v(7970, -11040) * mm});
            skLineSegment(sketch, "E481.9.0.3", {"start": v(7920, -11040) * mm, "end": v(7970, -11040) * mm});
            skLineSegment(sketch, "E481.10.0.0", {"start": v(8800, -10990) * mm, "end": v(8850, -10990) * mm});
            skLineSegment(sketch, "E481.10.0.1", {"start": v(8800, -10990) * mm, "end": v(8800, -11040) * mm});
            skLineSegment(sketch, "E481.10.0.2", {"start": v(8850, -10990) * mm, "end": v(8850, -11040) * mm});
            skLineSegment(sketch, "E481.10.0.3", {"start": v(8800, -11040) * mm, "end": v(8850, -11040) * mm});
            skLineSegment(sketch, "E481.11.0.0", {"start": v(9680, -10990) * mm, "end": v(9730, -10990) * mm});
            skLineSegment(sketch, "E481.11.0.1", {"start": v(9680, -10990) * mm, "end": v(9680, -11040) * mm});
            skLineSegment(sketch, "E481.11.0.2", {"start": v(9730, -10990) * mm, "end": v(9730, -11040) * mm});
            skLineSegment(sketch, "E481.11.0.3", {"start": v(9680, -11040) * mm, "end": v(9730, -11040) * mm});
            skLineSegment(sketch, "E481.12.0.0", {"start": v(10560, -10990) * mm, "end": v(10610, -10990) * mm});
            skLineSegment(sketch, "E481.12.0.1", {"start": v(10560, -10990) * mm, "end": v(10560, -11040) * mm});
            skLineSegment(sketch, "E481.12.0.2", {"start": v(10610, -10990) * mm, "end": v(10610, -11040) * mm});
            skLineSegment(sketch, "E481.12.0.3", {"start": v(10560, -11040) * mm, "end": v(10610, -11040) * mm});
            skLineSegment(sketch, "E481.13.0.0", {"start": v(11440, -10990) * mm, "end": v(11490, -10990) * mm});
            skLineSegment(sketch, "E481.13.0.1", {"start": v(11440, -10990) * mm, "end": v(11440, -11040) * mm});
            skLineSegment(sketch, "E481.13.0.2", {"start": v(11490, -10990) * mm, "end": v(11490, -11040) * mm});
            skLineSegment(sketch, "E481.13.0.3", {"start": v(11440, -11040) * mm, "end": v(11490, -11040) * mm});
            skLineSegment(sketch, "E481.14.0.0", {"start": v(12320, -10990) * mm, "end": v(12370, -10990) * mm});
            skLineSegment(sketch, "E481.14.0.1", {"start": v(12320, -10990) * mm, "end": v(12320, -11040) * mm});
            skLineSegment(sketch, "E481.14.0.2", {"start": v(12370, -10990) * mm, "end": v(12370, -11040) * mm});
            skLineSegment(sketch, "E481.14.0.3", {"start": v(12320, -11040) * mm, "end": v(12370, -11040) * mm});
            skLineSegment(sketch, "E481.15.0.0", {"start": v(13200, -10990) * mm, "end": v(13250, -10990) * mm});
            skLineSegment(sketch, "E481.15.0.1", {"start": v(13200, -10990) * mm, "end": v(13200, -11040) * mm});
            skLineSegment(sketch, "E481.15.0.2", {"start": v(13250, -10990) * mm, "end": v(13250, -11040) * mm});
            skLineSegment(sketch, "E481.15.0.3", {"start": v(13200, -11040) * mm, "end": v(13250, -11040) * mm});
            skLineSegment(sketch, "E481.16.0.0", {"start": v(14080, -10990) * mm, "end": v(14130, -10990) * mm});
            skLineSegment(sketch, "E481.16.0.1", {"start": v(14080, -10990) * mm, "end": v(14080, -11040) * mm});
            skLineSegment(sketch, "E481.16.0.2", {"start": v(14130, -10990) * mm, "end": v(14130, -11040) * mm});
            skLineSegment(sketch, "E481.16.0.3", {"start": v(14080, -11040) * mm, "end": v(14130, -11040) * mm});
            skLineSegment(sketch, "E481.17.0.0", {"start": v(14960, -10990) * mm, "end": v(15010, -10990) * mm});
            skLineSegment(sketch, "E481.17.0.1", {"start": v(14960, -10990) * mm, "end": v(14960, -11040) * mm});
            skLineSegment(sketch, "E481.17.0.2", {"start": v(15010, -10990) * mm, "end": v(15010, -11040) * mm});
            skLineSegment(sketch, "E481.17.0.3", {"start": v(14960, -11040) * mm, "end": v(15010, -11040) * mm});
            skLineSegment(sketch, "E481.18.0.0", {"start": v(15840, -10990) * mm, "end": v(15890, -10990) * mm});
            skLineSegment(sketch, "E481.18.0.1", {"start": v(15840, -10990) * mm, "end": v(15840, -11040) * mm});
            skLineSegment(sketch, "E481.18.0.2", {"start": v(15890, -10990) * mm, "end": v(15890, -11040) * mm});
            skLineSegment(sketch, "E481.18.0.3", {"start": v(15840, -11040) * mm, "end": v(15890, -11040) * mm});
            skLineSegment(sketch, "E481.19.0.0", {"start": v(16720, -10990) * mm, "end": v(16770, -10990) * mm});
            skLineSegment(sketch, "E481.19.0.1", {"start": v(16720, -10990) * mm, "end": v(16720, -11040) * mm});
            skLineSegment(sketch, "E481.19.0.2", {"start": v(16770, -10990) * mm, "end": v(16770, -11040) * mm});
            skLineSegment(sketch, "E481.19.0.3", {"start": v(16720, -11040) * mm, "end": v(16770, -11040) * mm});
            skLineSegment(sketch, "E481.20.0.0", {"start": v(17600, -10990) * mm, "end": v(17650, -10990) * mm});
            skLineSegment(sketch, "E481.20.0.1", {"start": v(17600, -10990) * mm, "end": v(17600, -11040) * mm});
            skLineSegment(sketch, "E481.20.0.2", {"start": v(17650, -10990) * mm, "end": v(17650, -11040) * mm});
            skLineSegment(sketch, "E481.20.0.3", {"start": v(17600, -11040) * mm, "end": v(17650, -11040) * mm});
            skLineSegment(sketch, "E481.direction1", {"start": v(0, -11040) * mm, "end": v(880, -11040) * mm, "construction": true});
            skLineSegment(sketch, "E482.1.0.0", {"start": v(38320, -10990) * mm, "end": v(38320, -11040) * mm});
            skLineSegment(sketch, "E482.1.0.1", {"start": v(38370, -10990) * mm, "end": v(38320, -10990) * mm});
            skLineSegment(sketch, "E482.1.0.2", {"start": v(38370, -11040) * mm, "end": v(38320, -11040) * mm});
            skLineSegment(sketch, "E482.1.0.3", {"start": v(38370, -10990) * mm, "end": v(38370, -11040) * mm});
            skLineSegment(sketch, "E482.2.0.0", {"start": v(37440, -10990) * mm, "end": v(37440, -11040) * mm});
            skLineSegment(sketch, "E482.2.0.1", {"start": v(37490, -10990) * mm, "end": v(37440, -10990) * mm});
            skLineSegment(sketch, "E482.2.0.2", {"start": v(37490, -11040) * mm, "end": v(37440, -11040) * mm});
            skLineSegment(sketch, "E482.2.0.3", {"start": v(37490, -10990) * mm, "end": v(37490, -11040) * mm});
            skLineSegment(sketch, "E482.3.0.0", {"start": v(36560, -10990) * mm, "end": v(36560, -11040) * mm});
            skLineSegment(sketch, "E482.3.0.1", {"start": v(36610, -10990) * mm, "end": v(36560, -10990) * mm});
            skLineSegment(sketch, "E482.3.0.2", {"start": v(36610, -11040) * mm, "end": v(36560, -11040) * mm});
            skLineSegment(sketch, "E482.3.0.3", {"start": v(36610, -10990) * mm, "end": v(36610, -11040) * mm});
            skLineSegment(sketch, "E482.4.0.0", {"start": v(35680, -10990) * mm, "end": v(35680, -11040) * mm});
            skLineSegment(sketch, "E482.4.0.1", {"start": v(35730, -10990) * mm, "end": v(35680, -10990) * mm});
            skLineSegment(sketch, "E482.4.0.2", {"start": v(35730, -11040) * mm, "end": v(35680, -11040) * mm});
            skLineSegment(sketch, "E482.4.0.3", {"start": v(35730, -10990) * mm, "end": v(35730, -11040) * mm});
            skLineSegment(sketch, "E482.5.0.0", {"start": v(34800, -10990) * mm, "end": v(34800, -11040) * mm});
            skLineSegment(sketch, "E482.5.0.1", {"start": v(34850, -10990) * mm, "end": v(34800, -10990) * mm});
            skLineSegment(sketch, "E482.5.0.2", {"start": v(34850, -11040) * mm, "end": v(34800, -11040) * mm});
            skLineSegment(sketch, "E482.5.0.3", {"start": v(34850, -10990) * mm, "end": v(34850, -11040) * mm});
            skLineSegment(sketch, "E482.6.0.0", {"start": v(33920, -10990) * mm, "end": v(33920, -11040) * mm});
            skLineSegment(sketch, "E482.6.0.1", {"start": v(33970, -10990) * mm, "end": v(33920, -10990) * mm});
            skLineSegment(sketch, "E482.6.0.2", {"start": v(33970, -11040) * mm, "end": v(33920, -11040) * mm});
            skLineSegment(sketch, "E482.6.0.3", {"start": v(33970, -10990) * mm, "end": v(33970, -11040) * mm});
            skLineSegment(sketch, "E482.7.0.0", {"start": v(33040, -10990) * mm, "end": v(33040, -11040) * mm});
            skLineSegment(sketch, "E482.7.0.1", {"start": v(33090, -10990) * mm, "end": v(33040, -10990) * mm});
            skLineSegment(sketch, "E482.7.0.2", {"start": v(33090, -11040) * mm, "end": v(33040, -11040) * mm});
            skLineSegment(sketch, "E482.7.0.3", {"start": v(33090, -10990) * mm, "end": v(33090, -11040) * mm});
            skLineSegment(sketch, "E482.8.0.0", {"start": v(32160, -10990) * mm, "end": v(32160, -11040) * mm});
            skLineSegment(sketch, "E482.8.0.1", {"start": v(32210, -10990) * mm, "end": v(32160, -10990) * mm});
            skLineSegment(sketch, "E482.8.0.2", {"start": v(32210, -11040) * mm, "end": v(32160, -11040) * mm});
            skLineSegment(sketch, "E482.8.0.3", {"start": v(32210, -10990) * mm, "end": v(32210, -11040) * mm});
            skLineSegment(sketch, "E482.9.0.0", {"start": v(31280, -10990) * mm, "end": v(31280, -11040) * mm});
            skLineSegment(sketch, "E482.9.0.1", {"start": v(31330, -10990) * mm, "end": v(31280, -10990) * mm});
            skLineSegment(sketch, "E482.9.0.2", {"start": v(31330, -11040) * mm, "end": v(31280, -11040) * mm});
            skLineSegment(sketch, "E482.9.0.3", {"start": v(31330, -10990) * mm, "end": v(31330, -11040) * mm});
            skLineSegment(sketch, "E482.10.0.0", {"start": v(30400, -10990) * mm, "end": v(30400, -11040) * mm});
            skLineSegment(sketch, "E482.10.0.1", {"start": v(30450, -10990) * mm, "end": v(30400, -10990) * mm});
            skLineSegment(sketch, "E482.10.0.2", {"start": v(30450, -11040) * mm, "end": v(30400, -11040) * mm});
            skLineSegment(sketch, "E482.10.0.3", {"start": v(30450, -10990) * mm, "end": v(30450, -11040) * mm});
            skLineSegment(sketch, "E482.11.0.0", {"start": v(29520, -10990) * mm, "end": v(29520, -11040) * mm});
            skLineSegment(sketch, "E482.11.0.1", {"start": v(29570, -10990) * mm, "end": v(29520, -10990) * mm});
            skLineSegment(sketch, "E482.11.0.2", {"start": v(29570, -11040) * mm, "end": v(29520, -11040) * mm});
            skLineSegment(sketch, "E482.11.0.3", {"start": v(29570, -10990) * mm, "end": v(29570, -11040) * mm});
            skLineSegment(sketch, "E482.12.0.0", {"start": v(28640, -10990) * mm, "end": v(28640, -11040) * mm});
            skLineSegment(sketch, "E482.12.0.1", {"start": v(28690, -10990) * mm, "end": v(28640, -10990) * mm});
            skLineSegment(sketch, "E482.12.0.2", {"start": v(28690, -11040) * mm, "end": v(28640, -11040) * mm});
            skLineSegment(sketch, "E482.12.0.3", {"start": v(28690, -10990) * mm, "end": v(28690, -11040) * mm});
            skLineSegment(sketch, "E482.13.0.0", {"start": v(27760, -10990) * mm, "end": v(27760, -11040) * mm});
            skLineSegment(sketch, "E482.13.0.1", {"start": v(27810, -10990) * mm, "end": v(27760, -10990) * mm});
            skLineSegment(sketch, "E482.13.0.2", {"start": v(27810, -11040) * mm, "end": v(27760, -11040) * mm});
            skLineSegment(sketch, "E482.13.0.3", {"start": v(27810, -10990) * mm, "end": v(27810, -11040) * mm});
            skLineSegment(sketch, "E482.14.0.0", {"start": v(26880, -10990) * mm, "end": v(26880, -11040) * mm});
            skLineSegment(sketch, "E482.14.0.1", {"start": v(26930, -10990) * mm, "end": v(26880, -10990) * mm});
            skLineSegment(sketch, "E482.14.0.2", {"start": v(26930, -11040) * mm, "end": v(26880, -11040) * mm});
            skLineSegment(sketch, "E482.14.0.3", {"start": v(26930, -10990) * mm, "end": v(26930, -11040) * mm});
            skLineSegment(sketch, "E482.15.0.0", {"start": v(26000, -10990) * mm, "end": v(26000, -11040) * mm});
            skLineSegment(sketch, "E482.15.0.1", {"start": v(26050, -10990) * mm, "end": v(26000, -10990) * mm});
            skLineSegment(sketch, "E482.15.0.2", {"start": v(26050, -11040) * mm, "end": v(26000, -11040) * mm});
            skLineSegment(sketch, "E482.15.0.3", {"start": v(26050, -10990) * mm, "end": v(26050, -11040) * mm});
            skLineSegment(sketch, "E482.16.0.0", {"start": v(25120, -10990) * mm, "end": v(25120, -11040) * mm});
            skLineSegment(sketch, "E482.16.0.1", {"start": v(25170, -10990) * mm, "end": v(25120, -10990) * mm});
            skLineSegment(sketch, "E482.16.0.2", {"start": v(25170, -11040) * mm, "end": v(25120, -11040) * mm});
            skLineSegment(sketch, "E482.16.0.3", {"start": v(25170, -10990) * mm, "end": v(25170, -11040) * mm});
            skLineSegment(sketch, "E482.17.0.0", {"start": v(24240, -10990) * mm, "end": v(24240, -11040) * mm});
            skLineSegment(sketch, "E482.17.0.1", {"start": v(24290, -10990) * mm, "end": v(24240, -10990) * mm});
            skLineSegment(sketch, "E482.17.0.2", {"start": v(24290, -11040) * mm, "end": v(24240, -11040) * mm});
            skLineSegment(sketch, "E482.17.0.3", {"start": v(24290, -10990) * mm, "end": v(24290, -11040) * mm});
            skLineSegment(sketch, "E482.18.0.0", {"start": v(23360, -10990) * mm, "end": v(23360, -11040) * mm});
            skLineSegment(sketch, "E482.18.0.1", {"start": v(23410, -10990) * mm, "end": v(23360, -10990) * mm});
            skLineSegment(sketch, "E482.18.0.2", {"start": v(23410, -11040) * mm, "end": v(23360, -11040) * mm});
            skLineSegment(sketch, "E482.18.0.3", {"start": v(23410, -10990) * mm, "end": v(23410, -11040) * mm});
            skLineSegment(sketch, "E482.19.0.0", {"start": v(22480, -10990) * mm, "end": v(22480, -11040) * mm});
            skLineSegment(sketch, "E482.19.0.1", {"start": v(22530, -10990) * mm, "end": v(22480, -10990) * mm});
            skLineSegment(sketch, "E482.19.0.2", {"start": v(22530, -11040) * mm, "end": v(22480, -11040) * mm});
            skLineSegment(sketch, "E482.19.0.3", {"start": v(22530, -10990) * mm, "end": v(22530, -11040) * mm});
            skLineSegment(sketch, "E482.20.0.0", {"start": v(21600, -10990) * mm, "end": v(21600, -11040) * mm});
            skLineSegment(sketch, "E482.20.0.1", {"start": v(21650, -10990) * mm, "end": v(21600, -10990) * mm});
            skLineSegment(sketch, "E482.20.0.2", {"start": v(21650, -11040) * mm, "end": v(21600, -11040) * mm});
            skLineSegment(sketch, "E482.20.0.3", {"start": v(21650, -10990) * mm, "end": v(21650, -11040) * mm});
            skLineSegment(sketch, "E482.direction1", {"start": v(39200, -11040) * mm, "end": v(38320, -11040) * mm, "construction": true});
            skSolve(sketch);
        }
        {
            var Q0;
            Q0=qSketchRegion(id+"F24",true);
            extrude(context, id + "F25", {"entities" : qUnion([Q0]), "depth" : 75 * mm, "offsetDistance" : 25 * mm});
        }
        {
            var Q0;
            Q0=makeQuery(id+"F25.opExtrude","CAP_FACE",FACE,{"disambiguationData":[OSD([sQuery(id+"F24.wireOp",EDGE,"E459.bottom"),sQuery(id+"F24.wireOp",EDGE,"E459.top"),sQuery(id+"F24.wireOp",EDGE,"E459.left"),sQuery(id+"F24.wireOp",EDGE,"E459.right")])],"isStart":false});
            var sketch = newSketch(context, id + "F26", { "sketchPlane" : qUnion([Q0])});
            skLineSegment(sketch, "E483.bottom", {"start": v(0, -9250) * mm, "end": v(50, -9250) * mm});
            skLineSegment(sketch, "E483.top", {"start": v(0, -11040) * mm, "end": v(50, -11040) * mm});
            skLineSegment(sketch, "E483.left", {"start": v(0, -9250) * mm, "end": v(0, -11040) * mm});
            skLineSegment(sketch, "E483.right", {"start": v(50, -9250) * mm, "end": v(50, -10990) * mm});
            skLineSegment(sketch, "E484.bottom", {"start": v(50, -10990) * mm, "end": v(18200, -10990) * mm});
            skLineSegment(sketch, "E484.top", {"start": v(50, -11040) * mm, "end": v(18250, -11040) * mm});
            skLineSegment(sketch, "E484.right", {"start": v(18250, -10990) * mm, "end": v(18250, -11040) * mm});
            skLineSegment(sketch, "E485.bottom", {"start": v(18200, -9250) * mm, "end": v(18250, -9250) * mm});
            skLineSegment(sketch, "E485.top", {"start": v(18200, -11040) * mm, "end": v(18250, -11040) * mm});
            skLineSegment(sketch, "E485.left", {"start": v(18200, -9250) * mm, "end": v(18200, -10990) * mm});
            skLineSegment(sketch, "E485.right", {"start": v(18250, -9250) * mm, "end": v(18250, -11040) * mm});
            skLineSegment(sketch, "E486.bottom", {"start": v(21000, -10990) * mm, "end": v(39200, -10990) * mm});
            skLineSegment(sketch, "E486.top", {"start": v(20950, -11040) * mm, "end": v(39200, -11040) * mm});
            skLineSegment(sketch, "E487.bottom", {"start": v(39200, -9250) * mm, "end": v(39250, -9250) * mm});
            skLineSegment(sketch, "E487.top", {"start": v(39200, -11040) * mm, "end": v(39250, -11040) * mm});
            skLineSegment(sketch, "E487.left", {"start": v(39200, -9250) * mm, "end": v(39200, -10990) * mm});
            skLineSegment(sketch, "E487.right", {"start": v(39250, -9250) * mm, "end": v(39250, -11040) * mm});
            skLineSegment(sketch, "E488", {"start": v(21000, -10990) * mm, "end": v(21000, -9250) * mm});
            skLineSegment(sketch, "E489", {"start": v(21000, -9250) * mm, "end": v(20950, -9250) * mm});
            skLineSegment(sketch, "E490", {"start": v(20950, -9250) * mm, "end": v(20950, -11040) * mm});
            skSolve(sketch);
        }
        {
            var Q0;
            Q0=qSketchRegion(id+"F26",true);
            extrude(context, id + "F27", {"entities" : qUnion([Q0]), "depth" : 50 * mm, "offsetDistance" : 25 * mm});
        }
    });
